FCSTD DOCUMENT  (FreeCAD 0.18.4R)
Label: CL260-Carrier-E3D-Titan
License: All rights reserved
LicenseURL: http://en.wikipedia.org/wiki/All_rights_reserved
objects: Sketcher::SketchObject×66, PartDesign::Pad×38, PartDesign::Plane×32, Part::Feature×21, PartDesign::Pocket×19, Part::Mirroring×19, PartDesign::Body×12, PartDesign::ShapeBinder×7, PartDesign::FeatureBase×6, PartDesign::Line×5, App::DocumentObjectGroup×4, Mesh::Feature×2, PartDesign::Mirrored×2, PartDesign::PolarPattern×2, App::Part×1, PartDesign::Fillet×1, PartDesign::Revolution×1, PartDesign::Groove×1
note: 291 computed .brp shape members not serialized (recipe doc carries the construction recipe); baked Part::Feature solids carry a one-line shape summary decoded from their .brp

FEATURE [Sketcher::SketchObject] Sketch  label="BaseSketch_XAxis"
  MapMode = 5
  Placement = pos=(0,0,0) rot=(0.57735,0.57735,0.57735;2.0944rad)
  Support = -> [YZ_Plane]
  expr: Constraints[1] = BaseDimensions.Constraints.Radius_Aussen_Achsenlagerkörper
  expr: Constraints[0] = Sketch003.Constraints.Radius_Achse
  sketch-geometry (1):
    g0: Circle CenterX=-11 CenterY=0 CenterZ=0 NormalX=0 NormalY=0 NormalZ=1 AngleXU=0 Radius=4
  constraints (3):
    c: Radius(g0) = 4
    c: DistanceX(g0,g-1) = 11
    c: PointOnObject(g0,g-1)
FEATURE [PartDesign::Line] DatumLine  label="X-Axis-DatumLine"
  AttacherType = Attacher::AttachEngineLine
  MapMode = 19
  Placement = pos=(-1.2408e-12,-11,1.242e-12) rot=(0.57735,0.57735,0.57735;2.0944rad)
  Support = -> [Sketch]
FEATURE [Sketcher::SketchObject] Sketch001  label="BaseSketch_YAxis"
  ExternalGeometry = -> [DatumLine]
  MapMode = 5
  Placement = pos=(0,0,0) rot=(1,0,0;1.5708rad)
  Support = -> [XZ_Plane]
  expr: Constraints[2] = BaseDimensions.Constraints.Abstand_HorizontalerAchsenabstand
  expr: Constraints[1] = BaseDimensions.Constraints.Abstand_VerticalerAchsenabstand
  expr: Constraints[0] = Sketch003.Constraints.Radius_Achse
  sketch-geometry (1):
    g0: Circle CenterX=-1 CenterY=-18 CenterZ=0 NormalX=0 NormalY=0 NormalZ=1 AngleXU=0 Radius=4
  constraints (3):
    c: Radius(g0) = 4
    c: DistanceY(g0,g-1) = 18
    c: DistanceX(g0,g-1) = 1
FEATURE [PartDesign::Line] DatumLine001  label="Y-Axis-DatumLine"
  AttacherType = Attacher::AttachEngineLine
  MapMode = 19
  Placement = pos=(-1,1.8545e-12,-18) rot=(1,0,0;1.5708rad)
  Support = -> [Sketch001]
FEATURE [Sketcher::SketchObject] Sketch003  label="BaseDimensions"
  MapMode = 5
  Support = -> [XY_Plane]
  sketch-geometry (15):
    g0: LineSegment [constr] StartX=-56.7363 StartY=18.8275 StartZ=0 EndX=-55.7363 EndY=18.8275 EndZ=0
    g1: LineSegment [constr] StartX=-54.0832 StartY=19.0838 StartZ=0 EndX=-54.0832 EndY=1.08377 EndZ=0
    g2: Circle [constr] CenterX=-26.2433 CenterY=17.2317 CenterZ=0 NormalX=0 NormalY=0 NormalZ=1 AngleXU=0 Radius=7.65
    g3: Circle [constr] CenterX=-26.2433 CenterY=17.2317 CenterZ=0 NormalX=0 NormalY=0 NormalZ=1 AngleXU=0 Radius=11
    g4: Circle [constr] CenterX=-26.2433 CenterY=17.2317 CenterZ=0 NormalX=0 NormalY=0 NormalZ=1 AngleXU=0 Radius=4
    g5: LineSegment [constr] StartX=-26.6458 StartY=-5.59924 StartZ=0 EndX=-2.64579 EndY=-5.59924 EndZ=0
    g6: LineSegment [constr] StartX=-23.9154 StartY=-12.201 StartZ=0 EndX=-21.4154 EndY=-12.201 EndZ=0
    g7: LineSegment [constr] StartX=-24.8331 StartY=-20.4604 StartZ=0 EndX=-21.8331 EndY=-20.4604 EndZ=0
    g8: Circle [constr] CenterX=-71.3028 CenterY=-13.3844 CenterZ=0 NormalX=0 NormalY=0 NormalZ=1 AngleXU=0 Radius=1.85
    g9: LineSegment [constr] StartX=-63.2198 StartY=35.4421 StartZ=0 EndX=-27.8698 EndY=35.4421 EndZ=0
    g10: LineSegment [constr] StartX=-62.0053 StartY=53.3997 StartZ=0 EndX=-12.0053 EndY=53.3997 EndZ=0
    g11: LineSegment [constr] StartX=-62.1011 StartY=68.6634 StartZ=0 EndX=-47.1011 EndY=68.6634 EndZ=0
    g12: LineSegment [constr] StartX=-62.8302 StartY=84.8991 StartZ=0 EndX=-39.3302 EndY=84.8991 EndZ=0
    g13: LineSegment [constr] StartX=-60.5898 StartY=95.611 StartZ=0 EndX=-50.5898 EndY=95.611 EndZ=0
    g14: Circle [constr] CenterX=-26.2433 CenterY=17.2317 CenterZ=0 NormalX=0 NormalY=0 NormalZ=1 AngleXU=0 Radius=7.7
  constraints (21):
    c: Radius(g2) = 7.65  'Radius_Igus_Innen_Y'
    c: Radius(g3) = 11  'Radius_Aussen_Achsenlagerkörper'
    c: Radius(g4) = 4  'Radius_Achse'
    c: DistanceY(g1,g1) = 18  'Abstand_VerticalerAchsenabstand'
    c: DistanceX(g0,g0) = 1  'Abstand_HorizontalerAchsenabstand'
    c: DistanceX(g5,g5) = 24  'Length_IgusBearing'
    c: DistanceX(g6,g6) = 2.5  'Thickness_Mountingbracket'
    c: DistanceX(g7,g7) = 3  'TitanMountPlate_ExtraThickness'
    c: Radius(g8) = 1.85  'Radius_Einpresshülse'
    c: Horizontal(g9)
    c: DistanceX(g9,g9) = 35.35  'Abstand_Löcher_TitanHalter'
    c: Horizontal(g10)
    c: DistanceX(g10,g10) = 50  'Länge_NemaHalter'
    c: Horizontal(g11)
    c: DistanceX(g11,g11) = 15  'Höhe_Lüfterwand'
    c: Horizontal(g12)
    c: DistanceX(g12,g12) = 23.5  'Länge_FanTisch'
    c: Horizontal(g13)
    c: DistanceX(g13,g13) = 10  'Länge_Überhang_FanTisch'
    c: Coincident(g14,g2)
    c: Radius(g14) = 7.7  'Radius_Igus_Innen_X'
FEATURE [Sketcher::SketchObject] Sketch004  label="YAchseBearingHolder"
  ExternalGeometry = -> [DatumLine001]
  MapMode = 5
  Placement = pos=(0,0,0) rot=(1,0,0;1.5708rad)
  Support = -> [XZ_Plane]
  expr: Constraints[1] = BaseDimensions.Constraints.Radius_Aussen_Achsenlagerkörper
  sketch-geometry (1):
    g0: Circle CenterX=-1 CenterY=-18 CenterZ=0 NormalX=0 NormalY=0 NormalZ=1 AngleXU=0 Radius=11
  constraints (2):
    c: Coincident(g0,g-3)
    c: Radius(g0) = 11
FEATURE [PartDesign::Pad] Pad  label="Pad_YAchseBearingHolder"
  Length = 48
  Length2 = 100
  Placement = pos=(0,0,0) rot=(1,0,0;1.5708rad)
  Profile = -> Sketch004
  Type = 0
  expr: Length = 2 * BaseDimensions.Constraints.Length_IgusBearing
FEATURE [Sketcher::SketchObject] Sketch005  label="XAchseBearingHolder"
  ExternalGeometry = -> [DatumLine]
  MapMode = 5
  Placement = pos=(0,0,0) rot=(0.57735,0.57735,0.57735;2.0944rad)
  Support = -> [YZ_Plane]
  expr: Constraints[1] = BaseDimensions.Constraints.Radius_Aussen_Achsenlagerkörper
  sketch-geometry (1):
    g0: Circle CenterX=-11 CenterY=0 CenterZ=0 NormalX=0 NormalY=0 NormalZ=1 AngleXU=0 Radius=11
  constraints (2):
    c: Coincident(g0,g-3)
    c: Radius(g0) = 11
FEATURE [PartDesign::Pad] Pad001  label="Pad_XAchseBearingHolder"
  BaseFeature = -> Pad
  Length = 48
  Length2 = 100
  Placement = pos=(0,0,0) rot=(1,0,0;1.5708rad)
  Profile = -> Sketch005
  Reversed = true
  Type = 0
  expr: Length = 2 * BaseDimensions.Constraints.Length_IgusBearing
FEATURE [PartDesign::Plane] DatumPlane  label="XAchseBearingHolderSeite1"
  Length = 30.3498
  MapMode = 11
  Placement = pos=(-1.2408e-12,-11,1.242e-12) rot=(0.707107,0,-0.707107;3.14159rad)
  ResizeMode = 0
  Support = -> [Sketch005]
  Width = 48.3498
FEATURE [Sketcher::SketchObject] Sketch006  label="Bracket"
  ExternalGeometry = -> [DatumLine]
  MapMode = 5
  Placement = pos=(-1.2408e-12,-11,1.242e-12) rot=(0.707107,0,-0.707107;3.14159rad)
  Support = -> [DatumPlane]
  expr: Constraints[9] = 2 * BaseDimensions.Constraints.Length_IgusBearing
  expr: Constraints[8] = BaseDimensions.Constraints.Radius_Aussen_Achsenlagerkörper
  expr: Constraints[4] = 2 * BaseDimensions.Constraints.Length_IgusBearing - BaseDimensions.Constraints.Radius_Aussen_Achsenlagerkörper
  sketch-geometry (4):
    g0: LineSegment StartX=10.8613 StartY=37 StartZ=0 EndX=-10.918 EndY=37 EndZ=0
    g1: LineSegment StartX=-10.918 StartY=37 StartZ=0 EndX=-10.918 EndY=-11 EndZ=0
    g2: LineSegment StartX=10.8613 StartY=-11 StartZ=0 EndX=10.8613 EndY=37 EndZ=0
    g3: LineSegment StartX=-10.918 StartY=-11 StartZ=0 EndX=10.8613 EndY=-11 EndZ=0
  constraints (10):
    c: Coincident(g0,g1)
    c: Coincident(g2,g0)
    c: Horizontal(g0)
    c: Vertical(g1)
    c: Vertical(g2) = 37
    c: Coincident(g3,g1)
    c: Coincident(g3,g2)
    c: Horizontal(g3)
    c: DistanceY(g2,g-1) = 11
    c: DistanceY(g2,g2) = 48
FEATURE [PartDesign::Pad] Pad002  label="Pad_Bracket"
  BaseFeature = -> Pad001
  Length = 2.5
  Length2 = 100
  Placement = pos=(0,0,0) rot=(1,0,0;1.5708rad)
  Profile = -> Sketch006
  Type = 0
  expr: Length = Sketch003.Constraints.Thickness_Mountingbracket
FEATURE [Sketcher::SketchObject] Sketch007
  ExternalGeometry = -> [DatumLine,DatumLine001]
  MapMode = 5
  Placement = pos=(-1.2408e-12,-11,1.242e-12) rot=(0.707107,0,-0.707107;3.14159rad)
  Support = -> [DatumPlane]
  expr: Constraints[10] = 1 * BaseDimensions.Constraints.Radius_Aussen_Achsenlagerkörper
  expr: Constraints[9] = BaseDimensions.Constraints.Radius_Aussen_Achsenlagerkörper
  expr: Constraints[8] = BaseDimensions.Constraints.Radius_Aussen_Achsenlagerkörper
  sketch-geometry (4):
    g0: LineSegment StartX=-11 StartY=11 StartZ=0 EndX=18 EndY=11 EndZ=0
    g1: LineSegment StartX=18 StartY=11 StartZ=0 EndX=18 EndY=-11 EndZ=0
    g2: LineSegment StartX=18 StartY=-11 StartZ=0 EndX=-11 EndY=-11 EndZ=0
    g3: LineSegment StartX=-11 StartY=-11 StartZ=0 EndX=-11 EndY=11 EndZ=0
  constraints (12):
    c: Coincident(g0,g1)
    c: Coincident(g1,g2)
    c: Coincident(g2,g3)
    c: Coincident(g3,g0)
    c: Horizontal(g0)
    c: Horizontal(g2)
    c: Vertical(g1)
    c: Vertical(g3)
    c: DistanceX(g0,g-3) = 11
    c: DistanceY(g-3,g0) = 11
    c: DistanceY(g2,g-3) = 11
    c: PointOnObject(g1,g-4)
FEATURE [PartDesign::Pad] Pad003  label="YAxisSupport"
  BaseFeature = -> Pad002
  Length = 12
  Length2 = 100
  Placement = pos=(0,0,0) rot=(1,0,0;1.5708rad)
  Profile = -> Sketch007
  Type = 0
  expr: Length = BaseDimensions.Constraints.Abstand_HorizontalerAchsenabstand + BaseDimensions.Constraints.Radius_Aussen_Achsenlagerkörper
FEATURE [Sketcher::SketchObject] Sketch008
  ExternalGeometry = -> [DatumLine]
  MapMode = 5
  Placement = pos=(0,0,0) rot=(0.57735,0.57735,0.57735;2.0944rad)
  Support = -> [YZ_Plane]
  expr: Constraints[11] = BaseDimensions.Constraints.Radius_Aussen_Achsenlagerkörper + BaseDimensions.Constraints.TitanMountPlate_ExtraThickness
  expr: Constraints[10] = BaseDimensions.Constraints.Radius_Aussen_Achsenlagerkörper
  expr: Constraints[9] = BaseDimensions.Constraints.Radius_Aussen_Achsenlagerkörper
  sketch-geometry (4):
    g0: LineSegment StartX=-22 StartY=14 StartZ=0 EndX=0 EndY=14 EndZ=0
    g1: LineSegment StartX=0 StartY=14 StartZ=0 EndX=0 EndY=0 EndZ=0
    g2: LineSegment StartX=0 StartY=0 StartZ=0 EndX=-22 EndY=0 EndZ=0
    g3: LineSegment StartX=-22 StartY=0 StartZ=0 EndX=-22 EndY=14 EndZ=0
  constraints (12):
    c: Coincident(g0,g1)
    c: Coincident(g1,g2)
    c: Coincident(g2,g3)
    c: Coincident(g3,g0)
    c: Horizontal(g0)
    c: Horizontal(g2)
    c: Vertical(g1)
    c: Vertical(g3)
    c: PointOnObject(g-3,g2)
    c: DistanceX(g2,g-3) = 11
    c: DistanceX(g-3,g1) = 11
    c: DistanceY(g1,g1) = 14
FEATURE [PartDesign::Pad] Pad004  label="TitanTable"
  BaseFeature = -> Pad003
  Length = 48
  Length2 = 100
  Placement = pos=(0,0,0) rot=(1,0,0;1.5708rad)
  Profile = -> Sketch008
  Reversed = true
  Type = 0
  expr: Length = 2 * BaseDimensions.Constraints.Length_IgusBearing
FEATURE [PartDesign::Plane] DatumPlane001  label="X-Support-End-DatumPlane"
  AttachmentOffset = pos=(0,0,48) rot=(0,0,1;0rad)
  Length = 30.3498
  MapMode = 9
  Placement = pos=(-48,-7,-4.6266e-12) rot=(0.707107,0,-0.707107;3.14159rad)
  ResizeMode = 0
  Support = -> [Sketch]
  Width = 48.3498
  expr: AttachmentOffset.Base.z = 2 * BaseDimensions.Constraints.Length_IgusBearing
FEATURE [Sketcher::SketchObject] Sketch009
  ExternalGeometry = -> [DatumLine]
  MapMode = 5
  Placement = pos=(-48,-7,-4.6266e-12) rot=(0.707107,0,-0.707107;3.14159rad)
  Support = -> [DatumPlane001]
  expr: Constraints[1] = Sketch003.Constraints.Radius_Igus_Innen_X
  sketch-geometry (1):
    g0: Circle CenterX=0 CenterY=4 CenterZ=0 NormalX=0 NormalY=0 NormalZ=1 AngleXU=0 Radius=7.7
  constraints (2):
    c: Coincident(g0,g-3)
    c: Radius(g0) = 7.7
FEATURE [PartDesign::Pocket] Pocket  label="Pocket_X-Bearing"
  BaseFeature = -> Pad004
  Length = 5
  Length2 = 100
  Placement = pos=(0,0,0) rot=(1,0,0;1.5708rad)
  Profile = -> Sketch009
  Type = 1
FEATURE [Sketcher::SketchObject] Sketch010
  ExternalGeometry = -> [DatumLine001]
  MapMode = 5
  Placement = pos=(0,0,0) rot=(1,0,0;1.5708rad)
  Support = -> [XZ_Plane]
  expr: Constraints[1] = Sketch003.Constraints.Radius_Igus_Innen_Y
  sketch-geometry (1):
    g0: Circle CenterX=-1 CenterY=-18 CenterZ=0 NormalX=0 NormalY=0 NormalZ=1 AngleXU=0 Radius=7.65
  constraints (2):
    c: Coincident(g0,g-3)
    c: Radius(g0) = 7.65
FEATURE [PartDesign::Pocket] Pocket001  label="Pocket_Y-Bearing"
  BaseFeature = -> Pocket
  Length = 5
  Length2 = 100
  Placement = pos=(0,0,0) rot=(1,0,0;1.5708rad)
  Profile = -> Sketch010
  Reversed = true
  Type = 1
FEATURE [PartDesign::Plane] DatumPlane002  label="TitanMountTable_DatumPlane"
  AttachmentOffset = pos=(0,0,14) rot=(0,0,1;0rad)
  Length = 55.1545
  MapMode = 3
  Placement = pos=(-2.8207e-12,-11,14) rot=(0,0,-1;1.5708rad)
  ResizeMode = 0
  Support = -> [DatumLine]
  Width = 116.154
  expr: AttachmentOffset.Base.z = BaseDimensions.Constraints.Radius_Aussen_Achsenlagerkörper + BaseDimensions.Constraints.TitanMountPlate_ExtraThickness
FEATURE [Sketcher::SketchObject] Sketch011
  ExternalGeometry = -> [DatumLine,Pocket001,DatumPlane001]
  MapMode = 5
  Placement = pos=(-2.8207e-12,-11,14) rot=(0,0,-1;1.5708rad)
  Support = -> [DatumPlane002]
  expr: Constraints[3] = BaseDimensions.Constraints.Radius_Einpresshülse
  sketch-geometry (5):
    g0: Circle CenterX=-7.4 CenterY=-6.325 CenterZ=0 NormalX=0 NormalY=0 NormalZ=1 AngleXU=0 Radius=1.85
    g1: Circle CenterX=-7.4 CenterY=-41.675 CenterZ=0 NormalX=0 NormalY=0 NormalZ=1 AngleXU=0 Radius=1.85
    g2: LineSegment [constr] StartX=-7.4 StartY=-6.325 StartZ=0 EndX=-7.4 EndY=-41.675 EndZ=0
    g3: LineSegment [constr] StartX=-7.4 StartY=-48 StartZ=0 EndX=-7.4 EndY=-41.675 EndZ=0
    g4: LineSegment [constr] StartX=-7.4 StartY=-6.325 StartZ=0 EndX=-7.4 EndY=0 EndZ=0
  constraints (14):
    c: Coincident(g0,g2)
    c: Coincident(g2,g1)
    c: Parallel(g2,g-3)
    c: Radius(g1) = 1.85
    c: Equal(g1,g0)
    c: DistanceY(g2,g2) = 35.35
    c: DistanceX(g-4,g0) = 3.6
    c: PointOnObject(g3,g-5)
    c: Vertical(g3)
    c: Coincident(g3,g1)
    c: Coincident(g4,g0)
    c: Vertical(g4)
    c: Equal(g4,g3)
    c: PointOnObject(g4,g-1)
FEATURE [PartDesign::Pocket] Pocket002  label="Titan_MountingHoles"
  BaseFeature = -> Pocket001
  Length = 8.5
  Length2 = 100
  Placement = pos=(0,0,0) rot=(1,0,0;1.5708rad)
  Profile = -> Sketch011
  Type = 0
FEATURE [Sketcher::SketchObject] Sketch012
  ExternalGeometry = -> [DatumPlane002,DatumLine]
  MapMode = 5
  Placement = pos=(-1.2408e-12,-11,1.242e-12) rot=(0.707107,0,-0.707107;3.14159rad)
  Support = -> [DatumPlane]
  expr: Constraints[9] = 2 * BaseDimensions.Constraints.Radius_Aussen_Achsenlagerkörper
  sketch-geometry (4):
    g0: LineSegment StartX=-14 StartY=11 StartZ=0 EndX=-11 EndY=11 EndZ=0
    g1: LineSegment StartX=-11 StartY=11 StartZ=0 EndX=-11 EndY=-11 EndZ=0
    g2: LineSegment StartX=-11 StartY=-11 StartZ=0 EndX=-14 EndY=-11 EndZ=0
    g3: LineSegment StartX=-14 StartY=-11 StartZ=0 EndX=-14 EndY=11 EndZ=0
  constraints (11):
    c: Coincident(g0,g1)
    c: Coincident(g1,g2)
    c: Coincident(g2,g3)
    c: Coincident(g3,g0)
    c: Horizontal(g0)
    c: Horizontal(g2)
    c: Vertical(g3)
    c: PointOnObject(g0,g-3)
    c: Symmetric(g1,g0,g-1)
    c: DistanceY(g1,g1) = 22
    c: DistanceX(g2,g2) = 3
FEATURE [Sketcher::SketchObject] Sketch013
  ExternalGeometry = -> [DatumPlane002,DatumLine]
  MapMode = 5
  Placement = pos=(-48,-7,-4.6266e-12) rot=(0.707107,0,-0.707107;3.14159rad)
  Support = -> [DatumPlane001]
  expr: Constraints[11] = BaseDimensions.Constraints.TitanMountPlate_ExtraThickness
  expr: Constraints[10] = 2 * BaseDimensions.Constraints.Radius_Aussen_Achsenlagerkörper
  expr: Constraints[9] = BaseDimensions.Constraints.Radius_Aussen_Achsenlagerkörper
  sketch-geometry (4):
    g0: LineSegment StartX=-14 StartY=15 StartZ=0 EndX=-11 EndY=15 EndZ=0
    g1: LineSegment StartX=-11 StartY=15 StartZ=0 EndX=-11 EndY=-7 EndZ=0
    g2: LineSegment StartX=-11 StartY=-7 StartZ=0 EndX=-14 EndY=-7 EndZ=0
    g3: LineSegment StartX=-14 StartY=-7 StartZ=0 EndX=-14 EndY=15 EndZ=0
  constraints (12):
    c: Coincident(g0,g1)
    c: Coincident(g1,g2)
    c: Coincident(g2,g3)
    c: Coincident(g3,g0)
    c: Horizontal(g0)
    c: Horizontal(g2)
    c: Vertical(g1)
    c: Vertical(g3)
    c: PointOnObject(g0,g-3)
    c: DistanceY(g-4,g0) = 11
    c: DistanceY(g1,g1) = 22
    c: DistanceX(g0,g0) = 3
FEATURE [Sketcher::SketchObject] Sketch014
  ExternalGeometry = -> [DatumLine001]
  MapMode = 5
  Placement = pos=(0,0,0) rot=(1,0,0;1.5708rad)
  Support = -> [XZ_Plane]
  expr: Constraints[10] = BaseDimensions.Constraints.Radius_Igus_Innen_Y + 2mm
  expr: Constraints[8] = BaseDimensions.Constraints.Radius_Aussen_Achsenlagerkörper
  sketch-geometry (4):
    g0: LineSegment StartX=11 StartY=-10.3416 StartZ=0 EndX=11 EndY=0 EndZ=0
    g1: LineSegment StartX=11 StartY=0 StartZ=0 EndX=0 EndY=0 EndZ=0
    g2: LineSegment StartX=0 StartY=0 StartZ=0 EndX=0 EndY=-8.40195 EndZ=0
    g3: LineSegment StartX=11 StartY=-10.3416 StartZ=0 EndX=0 EndY=-8.40195 EndZ=0
  constraints (11):
    c: Coincident(g0,g1)
    c: Coincident(g1,g2)
    c: Horizontal(g1)
    c: Vertical(g0)
    c: Vertical(g2)
    c: Coincident(g3,g0)
    c: Coincident(g3,g2)
    c: Coincident(g-1,g1)
    c: DistanceX(g1,g1) = 11
    c: Angle(g3,g2) = 1.74533
    c: Distance(g-3,g2) = 9.65
FEATURE [PartDesign::Pocket] Pocket003
  BaseFeature = -> Pocket002
  Length = 24
  Length2 = 100
  Placement = pos=(0,0,0) rot=(1,0,0;1.5708rad)
  Profile = -> Sketch014
  Reversed = true
  Type = 0
  expr: Length = 2mm + 2 * BaseDimensions.Constraints.Radius_Aussen_Achsenlagerkörper
FEATURE [Sketcher::SketchObject] Sketch016
  ExternalGeometry = -> [DatumLine001]
  MapMode = 5
  Placement = pos=(-1.2408e-12,-11,1.242e-12) rot=(0.707107,0,-0.707107;3.14159rad)
  Support = -> [DatumPlane]
  expr: Constraints[28] = BaseDimensions.Constraints.Radius_Aussen_Achsenlagerkörper
  expr: Constraints[10] = BaseDimensions.Constraints.Radius_Einpresshülse
  sketch-geometry (10):
    g0: LineSegment StartX=-3 StartY=34 StartZ=0 EndX=7 EndY=34 EndZ=0
    g1: LineSegment StartX=7 StartY=34 StartZ=0 EndX=7 EndY=14 EndZ=0
    g2: LineSegment StartX=7 StartY=14 StartZ=0 EndX=-3 EndY=14 EndZ=0
    g3: LineSegment StartX=-3 StartY=14 StartZ=0 EndX=-3 EndY=34 EndZ=0
    g4: Circle CenterX=-7 CenterY=33 CenterZ=0 NormalX=0 NormalY=0 NormalZ=1 AngleXU=0 Radius=1.85
    g5: Circle CenterX=-7 CenterY=27 CenterZ=0 NormalX=0 NormalY=0 NormalZ=1 AngleXU=0 Radius=1.85
    g6: Circle CenterX=-7 CenterY=21 CenterZ=0 NormalX=0 NormalY=0 NormalZ=1 AngleXU=0 Radius=1.85
    g7: Circle CenterX=-7 CenterY=15 CenterZ=0 NormalX=0 NormalY=0 NormalZ=1 AngleXU=0 Radius=1.85
    g8: LineSegment [constr] StartX=-7 StartY=34 StartZ=0 EndX=-7 EndY=14 EndZ=0
    g9: LineSegment [constr] StartX=7 StartY=34 StartZ=0 EndX=18 EndY=34 EndZ=0
  constraints (31):
    c: Coincident(g0,g1)
    c: Coincident(g1,g2)
    c: Coincident(g2,g3)
    c: Coincident(g3,g0)
    c: Horizontal(g0)
    c: Horizontal(g2)
    c: Vertical(g1)
    c: Vertical(g3)
    c: DistanceX(g0,g0) = 10
    c: DistanceY(g3,g3) = 20
    c: Radius(g7) = 1.85
    c: Equal(g7,g6)
    c: Equal(g7,g5)
    c: Equal(g7,g4)
    c: DistanceY(g5,g4) = 6
    c: DistanceY(g6,g5) = 6
    c: DistanceY(g7,g6) = 6
    c: Vertical(g8)
    c: PointOnObject(g7,g8)
    c: PointOnObject(g6,g8)
    c: PointOnObject(g5,g8)
    c: PointOnObject(g4,g8)
    c: DistanceY(g-1,g1) = 14
    c: DistanceY(g2,g7) = 1
    c: DistanceX(g7,g2) = 4
    c: Coincident(g9,g0)
    c: PointOnObject(g9,g-3)
    c: Horizontal(g9)
    c: DistanceX(g9,g9) = 11
    c: PointOnObject(g8,g0)
    c: PointOnObject(g8,g2)
FEATURE [PartDesign::Pocket] Pocket005  label="Fanduct-Holes"
  BaseFeature = -> Pocket003
  Length = 5
  Length2 = 100
  Placement = pos=(0,0,0) rot=(1,0,0;1.5708rad)
  Profile = -> Sketch016
  Reversed = true
  Type = 0
FEATURE [PartDesign::Plane] DatumPlane003  label="InnensSeite_X-AchsenBearingHalter"
  AttachmentOffset = pos=(0,0,22) rot=(0,0,1;0rad)
  Length = 112.944
  MapMode = 2
  Placement = pos=(0,-22,-2.2679e-12) rot=(1,0,0;1.5708rad)
  ResizeMode = 0
  Support = -> [Sketch001]
  Width = 33.9438
  expr: AttachmentOffset.Base.z = 2 * BaseDimensions.Constraints.Radius_Aussen_Achsenlagerkörper
FEATURE [Sketcher::SketchObject] Sketch017
  ExternalGeometry = -> [DatumLine,DatumPlane001]
  MapMode = 5
  Placement = pos=(0,-22,-2.2679e-12) rot=(1,0,0;1.5708rad)
  Support = -> [DatumPlane003]
  expr: Constraints[14] = 0.25mm + BaseDimensions.Constraints.Radius_Aussen_Achsenlagerkörper - BaseDimensions.Constraints.Radius_Einpresshülse
  expr: Constraints[0] = BaseDimensions.Constraints.Radius_Einpresshülse
  sketch-geometry (7):
    g0: Circle CenterX=-45.5 CenterY=9.4 CenterZ=0 NormalX=0 NormalY=0 NormalZ=1 AngleXU=0 Radius=1.85
    g1: Circle CenterX=-35.5 CenterY=9.4 CenterZ=0 NormalX=0 NormalY=0 NormalZ=1 AngleXU=0 Radius=1.85
    g2: Circle CenterX=-10.5 CenterY=9.4 CenterZ=0 NormalX=0 NormalY=0 NormalZ=1 AngleXU=0 Radius=1.85
    g3: Circle CenterX=-20.5 CenterY=9.4 CenterZ=0 NormalX=0 NormalY=0 NormalZ=1 AngleXU=0 Radius=1.85
    g4: LineSegment [constr] StartX=-45.5 StartY=9.4 StartZ=0 EndX=-45.5 EndY=-3.0003e-12 EndZ=0
    g5: LineSegment [constr] StartX=-45.5 StartY=9.4 StartZ=0 EndX=-10.5 EndY=9.4 EndZ=0
    g6: LineSegment [constr] StartX=-48 StartY=9.4 StartZ=0 EndX=-45.5 EndY=9.4 EndZ=0
  constraints (20):
    c: Radius(g2) = 1.85
    c: Equal(g2,g3)
    c: Equal(g2,g1)
    c: Equal(g2,g0)
    c: Coincident(g4,g0)
    c: PointOnObject(g4,g-3)
    c: Vertical(g4)
    c: Coincident(g5,g0)
    c: Coincident(g5,g2)
    c: Horizontal(g5)
    c: PointOnObject(g1,g5)
    c: PointOnObject(g3,g5)
    c: DistanceX(g0,g1) = 10
    c: DistanceX(g3,g2) = 10
    c: DistanceY(g4,g4) = 9.4
    c: DistanceX(g1,g3) = 15
    c: Horizontal(g6)
    c: PointOnObject(g6,g-4)
    c: Coincident(g6,g0)
    c: DistanceX(g6,g6) = 2.5
FEATURE [PartDesign::Pocket] Pocket006  label="MoreHoles"
  BaseFeature = -> Pocket005
  Length = 8
  Length2 = 100
  Placement = pos=(0,0,0) rot=(1,0,0;1.5708rad)
  Profile = -> Sketch017
  Type = 0
FEATURE [PartDesign::Line] DatumLine005
  AttacherType = Attacher::AttachEngineLine
  MapMode = 19
  Placement = pos=(-6.325,-3.6,14) rot=(0,0,1;4.71239rad)
  Support = -> [Sketch011]
FEATURE [PartDesign::Line] DatumLine006
  AttacherType = Attacher::AttachEngineLine
  MapMode = 19
  Placement = pos=(-41.675,-3.6,14) rot=(0,0,1;4.71239rad)
  Support = -> [Sketch011]
FEATURE [PartDesign::Plane] DatumPlane004  label="TitanHolderMiddlePlane"
  AttachmentOffset = pos=(0,0,-17.675) rot=(0,0,1;0rad)
  Length = 48.3498
  MapMode = 14
  Placement = pos=(-24,-3.6,14) rot=(-0.57735,0.57735,0.57735;4.18879rad)
  ResizeMode = 0
  Support = -> [DatumLine006,DatumLine005]
  Width = 30.3498
  expr: AttachmentOffset.Base.z = -BaseDimensions.Constraints.Abstand_Löcher_TitanHalter / 2
FEATURE [Sketcher::SketchObject] Sketch024
  ExternalGeometry = -> [DatumPlane001]
  MapMode = 5
  Placement = pos=(0,-22,-2.2679e-12) rot=(1,0,0;1.5708rad)
  Support = -> [DatumPlane003]
  sketch-geometry (4):
    g0: LineSegment StartX=-40 StartY=-7.75 StartZ=0 EndX=-12 EndY=-7.75 EndZ=0
    g1: LineSegment StartX=-12 StartY=-7.75 StartZ=0 EndX=-12 EndY=-15.056 EndZ=0
    g2: LineSegment StartX=-12 StartY=-15.056 StartZ=0 EndX=-40 EndY=-15.056 EndZ=0
    g3: LineSegment StartX=-40 StartY=-15.056 StartZ=0 EndX=-40 EndY=-7.75 EndZ=0
  constraints (11):
    c: Coincident(g0,g1)
    c: Coincident(g1,g2)
    c: Coincident(g2,g3)
    c: Coincident(g3,g0)
    c: Horizontal(g0)
    c: Horizontal(g2)
    c: Vertical(g1)
    c: Vertical(g3)
    c: DistanceX(g0,g0) = 28
    c: DistanceY(g0,g-1) = 7.75
    c: Distance(g0,g-3) = 8
FEATURE [PartDesign::Plane] DatumPlane005
  Length = 43.4822
  MapMode = 11
  Placement = pos=(-1,1.8545e-12,-18) rot=(0.57735,-0.57735,0.57735;2.0944rad)
  ResizeMode = 0
  Support = -> [Sketch004]
  Width = 114.482
FEATURE [Mesh::Feature] titan_aero_holder_v5
  Placement = pos=(-55,-32.5,4.1) rot=(-1,0,0;3.14159rad)
FEATURE [Part::Feature] _0mm_Fan001  label="50mm-Fan"
  Placement = pos=(-52,-22,24) rot=(0,-1,0;1.5708rad)
  shape: bbox 15 x 51.49 x 51.5 mm, 1034 faces, 0 solids (baked)
FEATURE [Sketcher::SketchObject] Sketch032
  MapMode = 5
  Placement = pos=(-1.2408e-12,-11,1.242e-12) rot=(0.707107,0,-0.707107;3.14159rad)
  Support = -> [DatumPlane]
  expr: Constraints[0] = BaseDimensions.Constraints.Radius_Aussen_Achsenlagerkörper - 1mm
  sketch-geometry (8):
    g0: Circle CenterX=0 CenterY=0 CenterZ=0 NormalX=0 NormalY=0 NormalZ=1 AngleXU=0 Radius=10
    g1: LineSegment StartX=0 StartY=6 StartZ=0 EndX=-5.19615 EndY=3 EndZ=0
    g2: LineSegment StartX=-5.19615 StartY=3 StartZ=0 EndX=-5.19615 EndY=-3 EndZ=0
    g3: LineSegment StartX=-5.19615 StartY=-3 StartZ=0 EndX=0 EndY=-6 EndZ=0
    g4: LineSegment StartX=0 StartY=-6 StartZ=0 EndX=5.19615 EndY=-3 EndZ=0
    g5: LineSegment StartX=5.19615 StartY=-3 StartZ=0 EndX=5.19615 EndY=3 EndZ=0
    g6: LineSegment StartX=5.19615 StartY=3 StartZ=0 EndX=0 EndY=6 EndZ=0
    g7: Circle [constr] CenterX=0 CenterY=0 CenterZ=0 NormalX=0 NormalY=0 NormalZ=1 AngleXU=0 Radius=6
  constraints (18):
    c: Radius(g0) = 10
    c: Coincident(g1,g2)
    c: Coincident(g2,g3)
    c: Coincident(g3,g4)
    c: Coincident(g4,g5)
    c: Coincident(g5,g6)
    c: Coincident(g6,g1)
    c: Equal(g1, g2-g6) x5
    c: PointOnObject(g1,g7)
    c: PointOnObject(g2,g7)
    c: PointOnObject(g3,g7)
    c: PointOnObject(g4,g7)
    c: PointOnObject(g5,g7)
    c: PointOnObject(g6,g7)
    c: Coincident(g7,g-1)
    c: Radius(g7) = 6
    c: Vertical(g5)
    c: Coincident(g0,g-1)
FEATURE [PartDesign::Pad] Pad014  label="Hexnut-Anschlag-BearingX"
  BaseFeature = -> Pocket006
  Length = 1.5
  Length2 = 100
  Placement = pos=(0,0,0) rot=(1,0,0;1.5708rad)
  Profile = -> Sketch032
  Type = 0
FEATURE [Sketcher::SketchObject] Sketch033
  ExternalGeometry = -> [DatumLine001]
  MapMode = 5
  Placement = pos=(0,0,0) rot=(1,0,0;1.5708rad)
  Support = -> [XZ_Plane]
  expr: Constraints[1] = BaseDimensions.Constraints.Radius_Aussen_Achsenlagerkörper - 2mm
  sketch-geometry (8):
    g0: Circle CenterX=-1 CenterY=-18 CenterZ=0 NormalX=0 NormalY=0 NormalZ=1 AngleXU=0 Radius=9
    g1: LineSegment StartX=-4 StartY=-23.1962 StartZ=0 EndX=2 EndY=-23.1962 EndZ=0
    g2: LineSegment StartX=2 StartY=-23.1962 StartZ=0 EndX=5 EndY=-18 EndZ=0
    g3: LineSegment StartX=5 StartY=-18 StartZ=0 EndX=2 EndY=-12.8038 EndZ=0
    g4: LineSegment StartX=2 StartY=-12.8038 StartZ=0 EndX=-4 EndY=-12.8038 EndZ=0
    g5: LineSegment StartX=-4 StartY=-12.8038 StartZ=0 EndX=-7 EndY=-18 EndZ=0
    g6: LineSegment StartX=-7 StartY=-18 StartZ=0 EndX=-4 EndY=-23.1962 EndZ=0
    g7: Circle [constr] CenterX=-1 CenterY=-18 CenterZ=0 NormalX=0 NormalY=0 NormalZ=1 AngleXU=0 Radius=6
  constraints (18):
    c: Coincident(g0,g-3)
    c: Radius(g0) = 9
    c: Coincident(g1,g2)
    c: Coincident(g2,g3)
    c: Coincident(g3,g4)
    c: Coincident(g4,g5)
    c: Coincident(g5,g6)
    c: Coincident(g6,g1)
    c: Equal(g1, g2-g6) x5
    c: PointOnObject(g1,g7)
    c: PointOnObject(g2,g7)
    c: PointOnObject(g3,g7)
    c: PointOnObject(g4,g7)
    c: PointOnObject(g5,g7)
    c: PointOnObject(g6,g7)
    c: Coincident(g7,g0)
    c: Radius(g7) = 6
    c: Horizontal(g4)
FEATURE [PartDesign::Pad] Pad015  label="Hexnut-Anschlag-BearingY"
  BaseFeature = -> Pad014
  Length = 1.5
  Length2 = 100
  Placement = pos=(0,0,0) rot=(1,0,0;1.5708rad)
  Profile = -> Sketch033
  Type = 0
FEATURE [PartDesign::Pocket] Pocket007003  label="Heatsink_EnhanceAirFlow"
  BaseFeature = -> Pad015
  Length = 5
  Length2 = 100
  Placement = pos=(0,0,0) rot=(1,0,0;1.5708rad)
  Profile = -> Sketch024
  Type = 1
FEATURE [Part::Feature] Part__Feature020  label="ISO 4762 - M3 x 25ISO"
  Placement = pos=(28.5171,-8.05,-25) rot=(0,-1,0;1.5708rad)
  shape: bbox 5.953 x 5.953 x 28 mm, 15 faces (baked)
FEATURE [Part::Feature] Part__Feature008  label="M_BEARING_MR95ZZ"
  Placement = pos=(22.2171,-38.5563,-4) rot=(0.707107,0.000752,0.707107;3.1431rad)
  shape: bbox 9.742 x 9.742 x 3 mm, 55 faces, 13 solids (baked)
FEATURE [Part::Feature] Part__Feature001  label="Spur Gear21"
  Placement = pos=(0,22,0) rot=(0,0,1;3.09399rad)
  shape: bbox 34 x 33.98 x 4 mm, 267 faces (baked)
FEATURE [Part::Feature] Part__Feature009  label="M_BEARING_SMR74ZZ"
  Placement = pos=(22.2171,-38.5563,-20.75) rot=(0,1,0;1.5708rad)
  shape: bbox 9.742 x 9.742 x 3 mm, 55 faces, 13 solids (baked)
FEATURE [Part::Feature] Part__Feature014  label="EX_PIGNION"
  Placement = pos=(6.66075,-23,-0.4) rot=(-0.998967,-0.032133,0.032133;1.57183rad)
  shape: bbox 12.06 x 11.99 x 9 mm, 97 faces (baked)
FEATURE [Part::Feature] Part__Feature003  label="EX_EXTRUDER_LID (Edition 4)_Public"
  Placement = pos=(0.461723,-9.23586,-22) rot=(1,0,0;3.14159rad)
  shape: bbox 46.39 x 49.51 x 137 mm, 484 faces (baked)
FEATURE [Part::Mirroring] Part__Mirroring016  label="Spur Gear21 (Mirror #17)"
  Base = (0,0,0)
  Normal = (0,0,1)
  Placement = pos=(-23.13,-60.51,-5.8) rot=(0,0,-1;0.04119rad)
  Source = -> Part__Feature001
FEATURE [Part::Feature] Part__Feature017  label="ISO 4762 - M3 x 20ISO002"
  Placement = pos=(22.1608,-38.5,-25) rot=(0,-1,0;1.5708rad)
  shape: bbox 5.953 x 5.953 x 23 mm, 15 faces (baked)
FEATURE [Part::Feature] Part__Feature018  label="ANSI B18.2.4.2M - M4x0.7 - 7"
  Placement = pos=(-12.4308,-46,-13.5) rot=(1,0,0;2.0944rad)
  shape: bbox 3.8 x 8.083 x 8.083 mm, 23 faces (baked)
FEATURE [Part::Feature] Part__Feature012  label="Titan Idler Tension Screw v6"
  Placement = pos=(-20.0892,-46,-13.5) rot=(0,0,1;0rad)
  shape: bbox 18 x 15 x 15 mm, 12 faces (baked)
FEATURE [Part::Mirroring] Part__Mirroring005  label="Titan Idler Tension Screw v6 (Mirror #6)"
  Base = (0,0,0)
  Normal = (1,0,0)
  Source = -> Part__Feature012
FEATURE [Part::Feature] Part__Feature006  label="EX_EXTRUDER_BODY_2"
  Placement = pos=(6.66075,-23,-1) rot=(1,0,0;3.14159rad)
  shape: bbox 46.57 x 60.21 x 24.06 mm, 338 faces (baked)
FEATURE [Part::Mirroring] Part__Mirroring001  label="EX_EXTRUDER_BODY_2 (Mirror #2)"
  Base = (0,0,0)
  Normal = (1,0,0)
  Source = -> Part__Feature006
FEATURE [Part::Feature] Part__Feature016  label="ISO 4762 - M3 x 20ISO001"
  Placement = pos=(-8.83925,-38.5,-25) rot=(0,-1,0;1.5708rad)
  shape: bbox 5.953 x 5.953 x 23 mm, 15 faces (baked)
FEATURE [Part::Mirroring] Part__Mirroring009  label="ISO 4762 - M3 x 20ISO001 (Mirror #10)"
  Base = (0,0,0)
  Normal = (1,0,0)
  Source = -> Part__Feature016
FEATURE [Part::Mirroring] Part__Mirroring013  label="ISO 4762 - M3 x 25ISO (Mirror #14)"
  Base = (0,0,0)
  Normal = (1,0,0)
  Source = -> Part__Feature020
FEATURE [Part::Feature] Part__Feature013  label="PTFE_HOLDER (Edition 2)"
  Placement = pos=(11.7608,-16.3,-23.5) rot=(-1,-2e-06,-2e-06;1.5708rad)
  shape: bbox 11.22 x 59.29 x 16.4 mm, 201 faces (baked)
FEATURE [Part::Feature] Part__Feature015  label="ISO 4762 - M3 x 20ISO"
  Placement = pos=(-8.83925,-7.5,-25) rot=(0,-1,0;1.5708rad)
  shape: bbox 5.953 x 5.953 x 23 mm, 15 faces (baked)
FEATURE [Part::Mirroring] Part__Mirroring008  label="ISO 4762 - M3 x 20ISO (Mirror #9)"
  Base = (0,0,0)
  Normal = (1,0,0)
  Source = -> Part__Feature015
FEATURE [Part::Feature] Part__Feature019  label="ISO 4762 - M3 x 5ISO"
  Placement = pos=(22.1608,-7.5,-3) rot=(0.447214,-0.774597,0.447214;1.82348rad)
  shape: bbox 5.75 x 5.75 x 8 mm, 15 faces (baked)
FEATURE [Part::Feature] Part__Feature021  label="EX_IDLER_PIN_3mm"
  Placement = pos=(12.2108,-39,-17.5) rot=(0,0,1;0rad)
  shape: bbox 3 x 3 x 8 mm, 8 faces (baked)
FEATURE [Part::Mirroring] Part__Mirroring007  label="EX_PIGNION (Mirror #8)"
  Base = (0,0,0)
  Normal = (1,0,0)
  Source = -> Part__Feature014
FEATURE [Part::Feature] Part__Feature010  label="SOLID001"
  shape: bbox 12.72 x 6.873 x 6.873 mm, 3 faces (baked)
FEATURE [Part::Mirroring] Part__Mirroring017  label="SOLID001 (Mirror #18)"
  Base = (0,0,0)
  Normal = (0,0,1)
  Placement = pos=(8,-45,-13) rot=(0,0,1;0rad)
  Source = -> Part__Feature010
FEATURE [Part::Feature] Part__Feature007  label="IC_EXTRUDER_IDLER_2.1"
  Placement = pos=(6.66075,-23,-11.5) rot=(0.57735,0.57735,-0.57735;4.18879rad)
  shape: bbox 22.05 x 46.43 x 9.747 mm, 528 faces (baked)
FEATURE [Part::Mirroring] Part__Mirroring006  label="PTFE_HOLDER (Edition 2) (Mirror #7)"
  Base = (0,0,0)
  Normal = (1,0,0)
  Source = -> Part__Feature013
FEATURE [Part::Mirroring] Part__Mirroring011  label="ANSI B18.2.4.2M - M4x0.7 - 7 (Mirror #12)"
  Base = (0,0,0)
  Normal = (1,0,0)
  Source = -> Part__Feature018
FEATURE [Part::Mirroring] Part__Mirroring010  label="ISO 4762 - M3 x 20ISO002 (Mirror #11)"
  Base = (0,0,0)
  Normal = (1,0,0)
  Source = -> Part__Feature017
FEATURE [Part::Mirroring] Part__Mirroring014  label="EX_IDLER_PIN_3mm (Mirror #15)"
  Base = (0,0,0)
  Normal = (1,0,0)
  Source = -> Part__Feature021
FEATURE [Part::Mirroring] Part__Mirroring  label="EX_EXTRUDER_LID (Edition 4)_Public (Mirror #1)"
  Base = (0,0,0)
  Normal = (1,0,0)
  Source = -> Part__Feature003
FEATURE [Part::Feature] Part__Feature  label="M_HOBB_v2_EX_Blank"
  Placement = pos=(-22.724,-4.52781,-6.8) rot=(0,0,-1;0.0774rad)
  shape: bbox 10.3 x 10.3 x 20.5 mm, 17 faces (baked)
FEATURE [Part::Mirroring] Part__Mirroring015  label="M_HOBB_v2_EX_Blank (Mirror #16)"
  Base = (0,0,0)
  Normal = (0,0,1)
  Placement = pos=(0.5,-34,-11) rot=(0,0,1;0rad)
  Source = -> Part__Feature
FEATURE [Part::Mirroring] Part__Mirroring002  label="IC_EXTRUDER_IDLER_2.1 (Mirror #3)"
  Base = (0,0,0)
  Normal = (1,0,0)
  Source = -> Part__Feature007
FEATURE [Part::Mirroring] Part__Mirroring004  label="M_BEARING_SMR74ZZ (Mirror #5)"
  Base = (0,0,0)
  Normal = (1,0,0)
  Source = -> Part__Feature009
FEATURE [Part::Mirroring] Part__Mirroring003  label="M_BEARING_MR95ZZ (Mirror #4)"
  Base = (0,0,0)
  Normal = (1,0,0)
  Source = -> Part__Feature008
FEATURE [Part::Mirroring] Part__Mirroring012  label="ISO 4762 - M3 x 5ISO (Mirror #13)"
  Base = (0,0,0)
  Normal = (1,0,0)
  Source = -> Part__Feature019
FEATURE [Part::Feature] Part__Feature011  label="COMPOUND001"
  shape: bbox 1.02 x 2e-07 x 1.02 mm, 0 faces, 0 solids (baked)
FEATURE [Part::Mirroring] Part__Mirroring018  label="COMPOUND001 (Mirror #19)"
  Base = (0,0,0)
  Normal = (0,0,1)
  Source = -> Part__Feature011
FEATURE [App::Part] Part  label="E3D-Titan_mirrored"
  Group = -> [Part__Feature003,Part__Mirroring,Part__Feature006,Part__Mirroring001,Part__Feature007,Part__Mirroring002,Part__Feature008,Part__Mirroring003,Part__Feature009,Part__Mirroring004,Part__Feature012,Part__Mirroring005,Part__Feature013,Part__Mirroring006,Part__Feature014,Part__Mirroring007,Part__Feature015,Part__Mirroring008,Part__Feature016,Part__Mirroring009,Part__Feature017,Part__Mirroring010,+16 more]
  License = CC BY 3.0
  LicenseURL = http://creativecommons.org/licenses/by/3.0/
  Origin = -> Origin005
  Placement = pos=(-17.2,-26.2,15) rot=(1,0,0;4.71239rad)
FEATURE [Part::Feature] Fusion001  label="E3DV6_Assembly"
  Placement = pos=(-35.0897,-39.6601,8.5) rot=(0,0.707107,0.707107;3.14159rad)
  shape: bbox 27.55 x 22.3 x 63.4 mm, 442 faces, 3 solids (baked)
FEATURE [PartDesign::Plane] DatumPlane020  label="Überhang_X_Tisch_TitanHalter"
  AttachmentOffset = pos=(0,0,4) rot=(0,0,1;0rad)
  Length = 30.3498
  MapMode = 11
  Placement = pos=(4,-11,1.6934e-12) rot=(0.707107,0,0.707107;3.14159rad)
  ResizeMode = 0
  Support = -> [Sketch]
  Width = 48.3498
FEATURE [PartDesign::Pad] Pad005  label="Überhang_Zu_FanWand"
  BaseFeature = -> Pocket007003
  Length = 4
  Length2 = 100
  Placement = pos=(0,0,0) rot=(1,0,0;1.5708rad)
  Profile = -> Sketch012
  Reversed = true
  Type = 3
  UpToFace = -> DatumPlane020 [Plane]
FEATURE [Sketcher::SketchObject] Sketch018
  ExternalGeometry = -> [DatumPlane020]
  MapMode = 5
  Placement = pos=(-2.8207e-12,-11,14) rot=(0,0,-1;1.5708rad)
  Support = -> [DatumPlane002]
  expr: Constraints[8] = 2 * BaseDimensions.Constraints.Radius_Aussen_Achsenlagerkörper
  sketch-geometry (4):
    g0: LineSegment StartX=-11 StartY=4 StartZ=0 EndX=11 EndY=4 EndZ=0
    g1: LineSegment StartX=11 StartY=4 StartZ=0 EndX=11 EndY=2 EndZ=0
    g2: LineSegment StartX=11 StartY=2 StartZ=0 EndX=-11 EndY=2 EndZ=0
    g3: LineSegment StartX=-11 StartY=2 StartZ=0 EndX=-11 EndY=4 EndZ=0
  constraints (11):
    c: Coincident(g0,g1)
    c: Coincident(g1,g2)
    c: Coincident(g2,g3)
    c: Coincident(g3,g0)
    c: Horizontal(g0)
    c: Vertical(g1)
    c: Vertical(g3)
    c: Symmetric(g2,g1,g-2)
    c: DistanceX(g2,g2) = 22
    c: DistanceY(g1,g1) = 2  'Dicke_Lüfterwand'
    c: PointOnObject(g0,g-3)
FEATURE [PartDesign::Plane] DatumPlane021  label="Überhang_X_Tisch_TitanHalter2"
  AttachmentOffset = pos=(0,0,52) rot=(0,0,1;0rad)
  Length = 48.3498
  MapMode = 2
  Placement = pos=(-52,5.8771e-12,-5.8771e-12) rot=(-0.57735,0.57735,0.57735;4.18879rad)
  ResizeMode = 0
  Support = -> [Sketch]
  Width = 30.3498
  expr: AttachmentOffset.Base.z = 2 * BaseDimensions.Constraints.Length_IgusBearing + 4mm
FEATURE [PartDesign::Pad] Pad006  label="Überhang_Zu_FanWand2"
  BaseFeature = -> Pad005
  Length = 4
  Length2 = 100
  Placement = pos=(0,0,0) rot=(1,0,0;1.5708rad)
  Profile = -> Sketch013
  Type = 3
  UpToFace = -> DatumPlane021
FEATURE [PartDesign::Pad] Pad007  label="Lüfterwand1"
  BaseFeature = -> Pad006
  Length = 15
  Length2 = 100
  Placement = pos=(0,0,0) rot=(1,0,0;1.5708rad)
  Profile = -> Sketch018
  Type = 0
  expr: Length = BaseDimensions.Constraints.Höhe_Lüfterwand
FEATURE [Sketcher::SketchObject] Sketch019
  ExternalGeometry = -> [DatumPlane004,DatumPlane021]
  MapMode = 5
  Placement = pos=(-2.8207e-12,-11,14) rot=(0,0,-1;1.5708rad)
  Support = -> [DatumPlane002]
  expr: Constraints[8] = Sketch018.Constraints.Dicke_Lüfterwand
  expr: Constraints[9] = 2 * BaseDimensions.Constraints.Radius_Aussen_Achsenlagerkörper
  sketch-geometry (4):
    g0: LineSegment StartX=-11 StartY=-50 StartZ=0 EndX=11 EndY=-50 EndZ=0
    g1: LineSegment StartX=11 StartY=-50 StartZ=0 EndX=11 EndY=-52 EndZ=0
    g2: LineSegment StartX=11 StartY=-52 StartZ=0 EndX=-11 EndY=-52 EndZ=0
    g3: LineSegment StartX=-11 StartY=-52 StartZ=0 EndX=-11 EndY=-50 EndZ=0
  constraints (11):
    c: Coincident(g0,g1)
    c: Coincident(g1,g2)
    c: Coincident(g2,g3)
    c: Coincident(g3,g0)
    c: Horizontal(g2)
    c: Vertical(g1)
    c: Vertical(g3)
    c: Symmetric(g0,g0,g-2)
    c: DistanceY(g1,g1) = 2
    c: DistanceX(g2,g2) = 22
    c: PointOnObject(g1,g-4)
FEATURE [PartDesign::Pad] Pad008  label="Lüfeterwand2"
  BaseFeature = -> Pad007
  Length = 15
  Length2 = 100
  Placement = pos=(0,0,0) rot=(1,0,0;1.5708rad)
  Profile = -> Sketch019
  Type = 0
  expr: Length = BaseDimensions.Constraints.Höhe_Lüfterwand
FEATURE [Sketcher::SketchObject] Sketch023
  ExternalGeometry = -> [DatumPlane004,DatumPlane020,DatumPlane021]
  MapMode = 5
  Placement = pos=(-2.8207e-12,-11,14) rot=(0,0,-1;1.5708rad)
  Support = -> [DatumPlane002]
  expr: Constraints[6] = Sketch018.Constraints.Dicke_Lüfterwand
  sketch-geometry (4):
    g0: LineSegment StartX=-40 StartY=2 StartZ=0 EndX=40 EndY=2 EndZ=0
    g1: LineSegment StartX=40 StartY=2 StartZ=0 EndX=40 EndY=-50 EndZ=0
    g2: LineSegment StartX=40 StartY=-50 StartZ=0 EndX=-40 EndY=-50 EndZ=0
    g3: LineSegment StartX=-40 StartY=-50 StartZ=0 EndX=-40 EndY=2 EndZ=0
  constraints (10):
    c: Coincident(g0,g1)
    c: Coincident(g1,g2)
    c: Coincident(g2,g3)
    c: Coincident(g3,g0)
    c: Horizontal(g2)
    c: Vertical(g3)
    c: Distance(g0,g-4) = 2
    c: Symmetric(g0,g1,g-3)
    c: DistanceX(g0,g0) = 80  '80'
    c: Symmetric(g0,g0,g-2)
FEATURE [Sketcher::SketchObject] Sketch051
  ExternalGeometry = -> [DatumPlane002]
  MapMode = 5
  Placement = pos=(4,-11,1.6934e-12) rot=(0.707107,0,0.707107;3.14159rad)
  Support = -> [DatumPlane020]
  expr: Constraints[9] = BaseDimensions.Constraints.Radius_Aussen_Achsenlagerkörper + BaseDimensions.Constraints.Länge_Überhang_FanTisch
  expr: Constraints[8] = BaseDimensions.Constraints.Radius_Aussen_Achsenlagerkörper
  sketch-geometry (4):
    g0: LineSegment StartX=17 StartY=21 StartZ=0 EndX=20 EndY=21 EndZ=0
    g1: LineSegment StartX=20 StartY=21 StartZ=0 EndX=20 EndY=-11 EndZ=0
    g2: LineSegment StartX=20 StartY=-11 StartZ=0 EndX=17 EndY=-11 EndZ=0
    g3: LineSegment StartX=17 StartY=-11 StartZ=0 EndX=17 EndY=21 EndZ=0
  constraints (12):
    c: Coincident(g0,g1)
    c: Coincident(g1,g2)
    c: Coincident(g2,g3)
    c: Coincident(g3,g0)
    c: Horizontal(g0)
    c: Horizontal(g2)
    c: Vertical(g1)
    c: Vertical(g3)
    c: DistanceY(g1,g-1) = 11
    c: DistanceY(g-1,g0) = 21
    c: Distance(g2,g-3) = 3
    c: DistanceX(g2,g1) = 3
FEATURE [PartDesign::Pad] Pad025  label="Lüftermountingtisch1"
  BaseFeature = -> Pad008
  Length = 23.5
  Length2 = 100
  Placement = pos=(0,0,0) rot=(1,0,0;1.5708rad)
  Profile = -> Sketch051
  Type = 0
  expr: Length = BaseDimensions.Constraints.Länge_FanTisch
FEATURE [Sketcher::SketchObject] Sketch052
  ExternalGeometry = -> [DatumPlane003]
  MapMode = 5
  Placement = pos=(-2.8207e-12,-11,14) rot=(0,0,-1;1.5708rad)
  Support = -> [DatumPlane002]
  expr: Constraints[6] = BaseDimensions.Constraints.Radius_Einpresshülse
  sketch-geometry (6):
    g0: LineSegment [constr] StartX=17 StartY=24 StartZ=0 EndX=17 EndY=0 EndZ=0
    g1: Circle CenterX=17 CenterY=9 CenterZ=0 NormalX=0 NormalY=0 NormalZ=1 AngleXU=0 Radius=1.85
    g2: Circle CenterX=17 CenterY=24 CenterZ=0 NormalX=0 NormalY=0 NormalZ=1 AngleXU=0 Radius=1.85
    g3: LineSegment [constr] StartX=17 StartY=24 StartZ=0 EndX=-5 EndY=24 EndZ=0
    g4: Circle CenterX=5 CenterY=24 CenterZ=0 NormalX=0 NormalY=0 NormalZ=1 AngleXU=0 Radius=1.85
    g5: Circle CenterX=-5 CenterY=24 CenterZ=0 NormalX=0 NormalY=0 NormalZ=1 AngleXU=0 Radius=1.85
  constraints (17):
    c: Vertical(g0)
    c: PointOnObject(g0,g-1)
    c: Distance(g0,g-3) = 6
    c: PointOnObject(g1,g0)
    c: DistanceY(g0,g1) = 9
    c: DistanceY(g1,g2) = 15
    c: Radius(g1) = 1.85
    c: Equal(g1,g2)
    c: Coincident(g0,g2)
    c: Coincident(g3,g0)
    c: Horizontal(g3)
    c: DistanceX(g3,g0) = 22
    c: PointOnObject(g4,g3)
    c: DistanceX(g3,g4) = 10
    c: Coincident(g5,g3)
    c: Equal(g2,g4)
    c: Equal(g5,g4)
FEATURE [Sketcher::SketchObject] Sketch027  label="Inteface_To_Fans"
  ExternalGeometry = -> [Sketch052,DatumPlane004,DatumPlane005,DatumPlane020,DatumPlane021]
  MapMode = 5
  Placement = pos=(-2.8207e-12,-11,14) rot=(0,0,-1;1.5708rad)
  Support = -> [DatumPlane002]
  expr: Constraints[39] = Lüftermountingtisch1.Length
  expr: Constraints[36] = 2 * BaseDimensions.Constraints.Radius_Aussen_Achsenlagerkörper + BaseDimensions.Constraints.Länge_Überhang_FanTisch
  expr: Constraints[0] = BaseDimensions.Constraints.Radius_Einpresshülse
  sketch-geometry (16):
    g0: Circle CenterX=-5 CenterY=24 CenterZ=0 NormalX=0 NormalY=0 NormalZ=1 AngleXU=0 Radius=1.85
    g1: Circle CenterX=5 CenterY=24 CenterZ=0 NormalX=0 NormalY=0 NormalZ=1 AngleXU=0 Radius=1.85
    g2: Circle CenterX=17 CenterY=24 CenterZ=0 NormalX=0 NormalY=0 NormalZ=1 AngleXU=0 Radius=1.85
    g3: Circle CenterX=17 CenterY=9 CenterZ=0 NormalX=0 NormalY=0 NormalZ=1 AngleXU=0 Radius=1.85
    g4: Circle CenterX=-5 CenterY=-72 CenterZ=0 NormalX=0 NormalY=0 NormalZ=1 AngleXU=0 Radius=1.85
    g5: Circle CenterX=5 CenterY=-72 CenterZ=0 NormalX=0 NormalY=0 NormalZ=1 AngleXU=0 Radius=1.85
    g6: Circle CenterX=17 CenterY=-72 CenterZ=0 NormalX=0 NormalY=0 NormalZ=1 AngleXU=0 Radius=1.85
    g7: Circle CenterX=17 CenterY=-57 CenterZ=0 NormalX=0 NormalY=0 NormalZ=1 AngleXU=0 Radius=1.85
    g8: LineSegment StartX=-11 StartY=-75.5 StartZ=0 EndX=21 EndY=-75.5 EndZ=0
    g9: LineSegment StartX=21 StartY=-75.5 StartZ=0 EndX=21 EndY=-52 EndZ=0
    g10: LineSegment StartX=21 StartY=-52 StartZ=0 EndX=-11 EndY=-52 EndZ=0
    g11: LineSegment StartX=-11 StartY=-52 StartZ=0 EndX=-11 EndY=-75.5 EndZ=0
    g12: LineSegment StartX=-11 StartY=27.5 StartZ=0 EndX=21 EndY=27.5 EndZ=0
    g13: LineSegment StartX=21 StartY=27.5 StartZ=0 EndX=21 EndY=4 EndZ=0
    g14: LineSegment StartX=21 StartY=4 StartZ=0 EndX=-11 EndY=4 EndZ=0
    g15: LineSegment StartX=-11 StartY=4 StartZ=0 EndX=-11 EndY=27.5 EndZ=0
  constraints (34):
    c: Radius(g0) = 1.85
    c: Equal(g0, g1-g7) x7
    c: Coincident(g8,g9)
    c: Coincident(g9,g10)
    c: Coincident(g10,g11)
    c: Coincident(g11,g8)
    c: Horizontal(g8)
    c: Horizontal(g10)
    c: Vertical(g9)
    c: Vertical(g11)
    c: Coincident(g12,g13)
    c: Coincident(g13,g14)
    c: Coincident(g14,g15)
    c: Coincident(g15,g12)
    c: Horizontal(g12)
    c: Horizontal(g14)
    c: Vertical(g13)
    c: Vertical(g15)
    c: PointOnObject(g13,g9)
    c: Coincident(g2,g-3)
    c: Coincident(g3,g-6)
    c: Coincident(g1,g-4)
    c: Coincident(g0,g-5)
    c: Symmetric(g3,g7,g-7)
    c: Symmetric(g6,g2,g-7)
    c: Symmetric(g5,g1,g-7)
    c: Symmetric(g4,g0,g-7)
    c: PointOnObject(g13,g-9)
    c: PointOnObject(g14,g-8)
    c: PointOnObject(g9,g-10)
    c: DistanceX(g12,g12) = 32
    c: Equal(g12,g8)
    c: Equal(g13,g9)
    c: DistanceY(g13,g13) = 23.5
FEATURE [PartDesign::ShapeBinder] ShapeBinder
  Placement = pos=(-2.821e-12,-11,14) rot=(0,0,-1;1.5708rad)
  Support = -> [Sketch027]
  TraceSupport = false
FEATURE [Sketcher::SketchObject] Sketch028
  ExternalGeometry = -> [ShapeBinder]
  MapMode = 5
  Support = -> [XY_Plane001]
  sketch-geometry (14):
    g0: Circle CenterX=-72 CenterY=-28 CenterZ=0 NormalX=0 NormalY=0 NormalZ=1 AngleXU=0 Radius=2.25
    g1: Circle CenterX=-72 CenterY=-16 CenterZ=0 NormalX=0 NormalY=0 NormalZ=1 AngleXU=0 Radius=2.25
    g2: Circle CenterX=-72 CenterY=-6 CenterZ=0 NormalX=0 NormalY=0 NormalZ=1 AngleXU=0 Radius=2.25
    g3: LineSegment StartX=-52 StartY=-32 StartZ=0 EndX=-75.5 EndY=-32 EndZ=0
    g4: LineSegment StartX=-75.5 StartY=-32 StartZ=0 EndX=-75.5 EndY=6.0005e-12 EndZ=0
    g5: LineSegment StartX=-75.5 StartY=6e-12 StartZ=0 EndX=-54 EndY=6e-12 EndZ=0
    g6: LineSegment StartX=-62 StartY=-7.01066 StartZ=0 EndX=-57 EndY=-7.01066 EndZ=0
    g7: LineSegment StartX=-57 StartY=-7.01066 StartZ=0 EndX=-57 EndY=-22.0107 EndZ=0
    g8: LineSegment StartX=-57 StartY=-22.0107 StartZ=0 EndX=-62 EndY=-22.0107 EndZ=0
    g9: LineSegment StartX=-62 StartY=-22.0107 StartZ=0 EndX=-62 EndY=-7.01066 EndZ=0
    g10: LineSegment StartX=-52 StartY=-32 StartZ=0 EndX=-52 EndY=-23.0107 EndZ=0
    g11: LineSegment StartX=-52 StartY=-23.0107 StartZ=0 EndX=-54 EndY=-23.0107 EndZ=0
    g12: LineSegment StartX=-54 StartY=-23.0107 StartZ=0 EndX=-54 EndY=6.0005e-12 EndZ=0
    g13: Circle CenterX=-57 CenterY=-28 CenterZ=0 NormalX=0 NormalY=0 NormalZ=1 AngleXU=0 Radius=2.25
  constraints (36):
    c: Coincident(g0,g-5)
    c: Coincident(g1,g-4)
    c: Coincident(g2,g-3)
    c: Radius(g0) = 2.25
    c: Equal(g0,g1)
    c: Equal(g0,g2)
    c: Coincident(g3,g4)
    c: Coincident(g4,g5)
    c: Horizontal(g3)
    c: Horizontal(g5)
    c: Vertical(g4)
    c: Coincident(g3,g-9)
    c: PointOnObject(g5,g-8)
    c: Coincident(g6,g7)
    c: Coincident(g7,g8)
    c: Coincident(g8,g9)
    c: Coincident(g9,g6)
    c: Horizontal(g6)
    c: Horizontal(g8)
    c: Vertical(g7)
    c: Vertical(g9)
    c: DistanceY(g7,g7) = 15
    c: DistanceX(g7,g-7) = 5
    c: DistanceX(g8,g8) = 5
    c: Coincident(g3,g10)
    c: Vertical(g10)
    c: Coincident(g10,g11)
    c: Horizontal(g11)
    c: Coincident(g11,g12)
    c: Vertical(g12)
    c: Coincident(g5,g12)
    c: Coincident(g-7,g3)
    c: DistanceX(g11,g11) = 2
    c: DistanceY(g11,g7) = 1
    c: Coincident(g13,g-6)
    c: Equal(g13,g0)
FEATURE [PartDesign::Pad] Pad012
  Length = 2
  Length2 = 100
  Profile = -> Sketch028
  Type = 0
FEATURE [Sketcher::SketchObject] Sketch029
  ExternalGeometry = -> [ShapeBinder]
  MapMode = 5
  Support = -> [XY_Plane001]
  sketch-geometry (4):
    g0: LineSegment StartX=-67.65 StartY=-1.75 StartZ=0 EndX=-70.15 EndY=-1.75 EndZ=0
    g1: LineSegment StartX=-70.15 StartY=-1.75 StartZ=0 EndX=-70.15 EndY=27.714 EndZ=0
    g2: LineSegment StartX=-70.15 StartY=27.714 StartZ=0 EndX=-67.65 EndY=27.714 EndZ=0
    g3: LineSegment StartX=-67.65 StartY=27.714 StartZ=0 EndX=-67.65 EndY=-1.75 EndZ=0
  constraints (11):
    c: Coincident(g0,g1)
    c: Coincident(g1,g2)
    c: Coincident(g2,g3)
    c: Coincident(g3,g0)
    c: Horizontal(g0)
    c: Horizontal(g2)
    c: Vertical(g1)
    c: Vertical(g3)
    c: DistanceX(g2,g2) = 2.5
    c: DistanceX(g-3,g0) = 5.35
    c: DistanceY(g-3,g0) = -1.75
FEATURE [PartDesign::Pad] Pad013
  BaseFeature = -> Pad012
  Length = 16
  Length2 = 100
  Profile = -> Sketch029
  Type = 0
FEATURE [PartDesign::Plane] DatumPlane006
  AttachmentOffset = pos=(0,0,0) rot=(0,1,0;1.5708rad)
  Length = 67.5946
  MapMode = 7
  Placement = pos=(-70.15,-1.75,0) rot=(0.57735,0.57735,0.57735;2.0944rad)
  ResizeMode = 0
  Support = -> [Sketch029]
  Width = 33.8805
FEATURE [Sketcher::SketchObject] Sketch030
  MapMode = 5
  Placement = pos=(-70.15,-1.75,0) rot=(0.57735,0.57735,0.57735;2.0944rad)
  Support = -> [DatumPlane006]
  sketch-geometry (1):
    g0: Circle CenterX=24.4148 CenterY=10.9837 CenterZ=0 NormalX=0 NormalY=0 NormalZ=1 AngleXU=0 Radius=2.5
  constraints (1):
    c: Radius(g0) = 2.5
FEATURE [PartDesign::Pocket] Pocket007005
  BaseFeature = -> Pad013
  Length = 5
  Length2 = 100
  Profile = -> Sketch030
  Reversed = true
  Type = 1
FEATURE [PartDesign::Plane] DatumPlane007
  AttachmentOffset = pos=(0,0,0) rot=(0,1,0;1.5708rad)
  Length = 94.9297
  MapMode = 7
  Placement = pos=(-52,-32,0) rot=(0,0.707107,0.707107;3.14159rad)
  ResizeMode = 0
  Support = -> [Sketch028]
  Width = 35.4297
FEATURE [PartDesign::ShapeBinder] ShapeBinder001
  Placement = pos=(-2.821e-12,-11,14) rot=(0,0,-1;1.5708rad)
  Support = -> [Sketch027]
  TraceSupport = false
FEATURE [Sketcher::SketchObject] Sketch036
  ExternalGeometry = -> [ShapeBinder001]
  MapMode = 5
  Support = -> [XY_Plane002]
  sketch-geometry (9):
    g0: Circle CenterX=-72 CenterY=-16 CenterZ=0 NormalX=0 NormalY=0 NormalZ=1 AngleXU=0 Radius=2.25
    g1: Circle CenterX=-72 CenterY=-28 CenterZ=0 NormalX=0 NormalY=0 NormalZ=1 AngleXU=0 Radius=2.25
    g2: Circle CenterX=-57 CenterY=-28 CenterZ=0 NormalX=0 NormalY=0 NormalZ=1 AngleXU=0 Radius=2.25
    g3: LineSegment StartX=-75.5 StartY=-11 StartZ=0 EndX=-68 EndY=-11 EndZ=0
    g4: LineSegment StartX=-68 StartY=-11 StartZ=0 EndX=-68 EndY=-22.5 EndZ=0
    g5: LineSegment StartX=-68 StartY=-22.5 StartZ=0 EndX=-52 EndY=-22.5 EndZ=0
    g6: LineSegment StartX=-52 StartY=-22.5 StartZ=0 EndX=-52 EndY=-32 EndZ=0
    g7: LineSegment StartX=-52 StartY=-32 StartZ=0 EndX=-75.5 EndY=-32 EndZ=0
    g8: LineSegment StartX=-75.5 StartY=-32 StartZ=0 EndX=-75.5 EndY=-11 EndZ=0
  constraints (21):
    c: Coincident(g0,g-4)
    c: Coincident(g1,g-5)
    c: Coincident(g2,g-6)
    c: Radius(g1) = 2.25
    c: Equal(g1,g0)
    c: Equal(g1,g2)
    c: PointOnObject(g3,g-7)
    c: Coincident(g3,g4)
    c: Vertical(g4)
    c: Coincident(g4,g5)
    c: Horizontal(g5)
    c: Coincident(g5,g6)
    c: Vertical(g6)
    c: Coincident(g6,g7)
    c: Coincident(g7,g8)
    c: Coincident(g8,g3)
    c: Symmetric(g0,g-3,g3)
    c: Coincident(g7,g-9)
    c: Coincident(g6,g-10)
    c: DistanceX(g5,g5) = 16
    c: Distance(g6) = 9.5  'FrontPartLength'
FEATURE [PartDesign::Pad] Pad016
  Length = 2.25
  Length2 = 100
  Profile = -> Sketch036
  Type = 0
FEATURE [PartDesign::Plane] DatumPlane009
  AttachmentOffset = pos=(0,0,0) rot=(0,1,0;1.5708rad)
  Length = 112.944
  MapMode = 7
  Placement = pos=(-68,-22.5,0) rot=(1,0,0;1.5708rad)
  ResizeMode = 0
  Support = -> [Sketch036]
  Width = 33.9438
FEATURE [Sketcher::SketchObject] Sketch037
  ExternalGeometry = -> [Sketch036]
  MapMode = 5
  Placement = pos=(-68,-22.5,0) rot=(1,0,0;1.5708rad)
  Support = -> [DatumPlane009]
  sketch-geometry (4):
    g0: LineSegment StartX=14 StartY=2.25 StartZ=0 EndX=3 EndY=2.25 EndZ=0
    g1: LineSegment StartX=3 StartY=2.25 StartZ=0 EndX=3 EndY=1.25 EndZ=0
    g2: LineSegment StartX=3 StartY=1.25 StartZ=0 EndX=14 EndY=1.25 EndZ=0
    g3: LineSegment StartX=14 StartY=1.25 StartZ=0 EndX=14 EndY=2.25 EndZ=0
  constraints (12):
    c: Coincident(g0,g1)
    c: Coincident(g1,g2)
    c: Coincident(g2,g3)
    c: Coincident(g3,g0)
    c: Horizontal(g0)
    c: Horizontal(g2)
    c: Vertical(g1)
    c: Vertical(g3)
    c: DistanceY(g-3,g2) = 1.25
    c: DistanceY(g3,g3) = 1
    c: DistanceX(g0,g0) = 11
    c: DistanceX(g2,g-3) = 2
FEATURE [PartDesign::Pad] Pad017
  BaseFeature = -> Pad016
  Length = 10
  Length2 = 100
  Profile = -> Sketch037
  Reversed = true
  Type = 0
FEATURE [PartDesign::Plane] DatumPlane010
  AttachmentOffset = pos=(0,0,2.25) rot=(0,0,1;0rad)
  Length = 116.154
  MapMode = 2
  Placement = pos=(0,0,2.25) rot=(0,0,1;0rad)
  ResizeMode = 0
  Support = -> [Sketch036]
  Width = 55.1545
  expr: AttachmentOffset.Base.z = Pad016.Length
FEATURE [Sketcher::SketchObject] Sketch038
  ExternalGeometry = -> [Sketch036]
  MapMode = 5
  Placement = pos=(0,0,2.25) rot=(0,0,1;0rad)
  Support = -> [DatumPlane010]
  sketch-geometry (4):
    g0: LineSegment StartX=-67.25 StartY=-22.5 StartZ=0 EndX=-52 EndY=-22.5 EndZ=0
    g1: LineSegment StartX=-52 StartY=-22.5 StartZ=0 EndX=-52 EndY=-32 EndZ=0
    g2: LineSegment StartX=-52 StartY=-32 StartZ=0 EndX=-67.25 EndY=-32 EndZ=0
    g3: LineSegment StartX=-67.25 StartY=-32 StartZ=0 EndX=-67.25 EndY=-22.5 EndZ=0
  constraints (12):
    c: Coincident(g0,g1)
    c: Coincident(g1,g2)
    c: Coincident(g2,g3)
    c: Coincident(g3,g0)
    c: Horizontal(g0)
    c: Horizontal(g2)
    c: Vertical(g1)
    c: Vertical(g3)
    c: PointOnObject(g0,g-3)
    c: PointOnObject(g1,g-4)
    c: DistanceX(g-3,g0) = 0.75
    c: DistanceX(g0,g-3) = 0
FEATURE [PartDesign::Pad] Pad018
  BaseFeature = -> Pad017
  Length = 17.25
  Length2 = 100
  Profile = -> Sketch038
  Type = 0
  expr: Length = 19.5mm - Pad016.Length
FEATURE [Sketcher::SketchObject] Sketch039
  ExternalGeometry = -> [Sketch038]
  MapMode = 5
  Placement = pos=(-68,-22.5,0) rot=(1,0,0;1.5708rad)
  Support = -> [DatumPlane009]
  expr: Constraints[11] = Pad018.Length - Sketch039.Constraints.WallThickness
  expr: Constraints[10] = Sketch039.Constraints.WallThickness + 0.5mm
  sketch-geometry (4):
    g0: LineSegment StartX=2.25 StartY=2.25 StartZ=0 EndX=14 EndY=2.25 EndZ=0
    g1: LineSegment StartX=14 StartY=2.25 StartZ=0 EndX=14 EndY=18 EndZ=0
    g2: LineSegment StartX=14 StartY=18 StartZ=0 EndX=2.25 EndY=18 EndZ=0
    g3: LineSegment StartX=2.25 StartY=18 StartZ=0 EndX=2.25 EndY=2.25 EndZ=0
  constraints (12):
    c: Coincident(g0,g1)
    c: Coincident(g1,g2)
    c: Coincident(g2,g3)
    c: Coincident(g3,g0)
    c: Horizontal(g0)
    c: Horizontal(g2)
    c: Vertical(g1)
    c: Vertical(g3)
    c: PointOnObject(g0,g-5)
    c: DistanceX(g-5,g0) = 1.5  'WallThickness'
    c: DistanceX(g0,g-5) = 2
    c: DistanceY(g3,g3) = 15.75
FEATURE [PartDesign::Pocket] Pocket007008
  BaseFeature = -> Pad018
  Length = 5
  Length2 = 100
  Profile = -> Sketch039
  Reversed = true
  Type = 1
FEATURE [PartDesign::Plane] DatumPlane011
  AttachmentOffset = pos=(0,0,0) rot=(0,1,0;1.5708rad)
  Length = 48.3498
  MapMode = 45
  Placement = pos=(-52,-27.25,2.25) rot=(-0.57735,0.57735,0.57735;4.18879rad)
  ResizeMode = 0
  Support = -> [Sketch038]
  Width = 30.3498
FEATURE [Sketcher::SketchObject] Sketch040
  MapMode = 5
  Placement = pos=(-52,-27.25,2.25) rot=(0.57735,-0.57735,-0.57735;2.0944rad)
  Support = -> [DatumPlane011]
  expr: Constraints[1] = Pad018.Length / 2
  sketch-geometry (1):
    g0: Circle CenterX=0 CenterY=8.625 CenterZ=0 NormalX=0 NormalY=0 NormalZ=1 AngleXU=0 Radius=1
  constraints (3):
    c: PointOnObject(g0,g-2)
    c: DistanceY(g-1,g0) = 8.625
    c: Radius(g0) = 1
FEATURE [PartDesign::Pocket] Pocket007009
  BaseFeature = -> Pocket007008
  Length = 5
  Length2 = 100
  Profile = -> Sketch040
  Reversed = true
  Type = 1
FEATURE [PartDesign::Plane] DatumPlane012
  AttachmentOffset = pos=(0,0,0) rot=(0,1,0;1.5708rad)
  Length = 67.5946
  MapMode = 7
  Placement = pos=(-70.15,-1.75,0) rot=(0.57735,0.57735,0.57735;2.0944rad)
  ResizeMode = 0
  Support = -> [Sketch029]
  Width = 33.8805
FEATURE [Sketcher::SketchObject] Sketch041
  MapMode = 5
  Placement = pos=(-70.15,-1.75,0) rot=(0.57735,0.57735,0.57735;2.0944rad)
  Support = -> [DatumPlane012]
  sketch-geometry (3):
    g0: LineSegment StartX=-2.3261 StartY=2.49481 StartZ=0 EndX=28.9441 EndY=20.4569 EndZ=0
    g1: LineSegment StartX=28.9441 StartY=20.4569 StartZ=0 EndX=-2.3261 EndY=20.4569 EndZ=0
    g2: LineSegment StartX=-2.3261 StartY=20.4569 StartZ=0 EndX=-2.3261 EndY=2.49481 EndZ=0
  constraints (6):
    c: PointOnObject(g1,g0)
    c: Coincident(g1,g2)
    c: Coincident(g0,g2)
    c: Vertical(g2)
    c: Horizontal(g1)
    c: Coincident(g0,g1)
FEATURE [PartDesign::Pocket] Pocket007010
  BaseFeature = -> Pocket007005
  Length = 5
  Length2 = 100
  Profile = -> Sketch041
  Reversed = true
  Type = 0
FEATURE [PartDesign::Body] Body001  label="Left-Fan-Clamp1-design"
  Group = -> [ShapeBinder,Sketch028,Pad012,Sketch029,Pad013,DatumPlane006,Sketch030,Pocket007005,DatumPlane007,DatumPlane012,Sketch041,Pocket007010]
  Origin = -> Origin001
  Placement = pos=(0,0,20) rot=(0,0,1;0rad)
  Tip = -> Pocket007010
FEATURE [PartDesign::Plane] DatumPlane013
  Length = 112.944
  MapMode = 2
  Placement = pos=(-68,-22.5,0) rot=(1,0,0;1.5708rad)
  ResizeMode = 0
  Support = -> [Sketch039]
  Width = 33.9438
FEATURE [Sketcher::SketchObject] Sketch042
  ExternalGeometry = -> [Sketch039]
  MapMode = 5
  Placement = pos=(-68,-22.5,0) rot=(1,0,0;1.5708rad)
  Support = -> [DatumPlane013]
  expr: Constraints[21] = Sketch042.Constraints.WallThickness
  expr: Constraints[20] = Sketch042.Constraints.WallThickness
  sketch-geometry (8):
    g0: LineSegment StartX=14.5 StartY=18.5 StartZ=0 EndX=14.5 EndY=2.25 EndZ=0
    g1: LineSegment StartX=1.75 StartY=2.25 StartZ=0 EndX=1.75 EndY=18.5 EndZ=0
    g2: LineSegment StartX=14 StartY=18 StartZ=0 EndX=14 EndY=2.25 EndZ=0
    g3: LineSegment StartX=2.25 StartY=2.25 StartZ=0 EndX=2.25 EndY=18 EndZ=0
    g4: LineSegment StartX=1.75 StartY=2.25 StartZ=0 EndX=2.25 EndY=2.25 EndZ=0
    g5: LineSegment StartX=14 StartY=2.25 StartZ=0 EndX=14.5 EndY=2.25 EndZ=0
    g6: LineSegment StartX=1.75 StartY=18.5 StartZ=0 EndX=14.5 EndY=18.5 EndZ=0
    g7: LineSegment StartX=2.25 StartY=18 StartZ=0 EndX=14 EndY=18 EndZ=0
  constraints (23):
    c: Vertical(g0)
    c: Vertical(g1)
    c: Vertical(g2)
    c: Vertical(g3)
    c: PointOnObject(g-4,g2)
    c: Coincident(g4,g1)
    c: Coincident(g4,g3)
    c: Horizontal(g4)
    c: Coincident(g5,g2)
    c: Coincident(g5,g0)
    c: Horizontal(g5)
    c: DistanceY(g2,g-4) = 0
    c: DistanceY(g3,g-5) = 0
    c: Coincident(g6,g1)
    c: Coincident(g6,g0)
    c: Horizontal(g6)
    c: Coincident(g7,g3)
    c: Coincident(g7,g2)
    c: Horizontal(g7)
    c: DistanceX(g1,g3) = 0.5  'WallThickness'
    c: DistanceX(g2,g0) = 0.5
    c: DistanceY(g2,g0) = 0.5
    c: Coincident(g3,g-5)
FEATURE [PartDesign::Pad] Pad019
  BaseFeature = -> Pocket007009
  Length = 5
  Length2 = 100
  Profile = -> Sketch042
  Reversed = true
  Type = 0
FEATURE [PartDesign::Plane] DatumPlane014
  AttachmentOffset = pos=(0,0,5) rot=(0,0,1;0rad)
  Length = 112.944
  MapMode = 2
  Placement = pos=(-68,-17.5,1.1e-15) rot=(0,0.707107,0.707107;3.14159rad)
  ResizeMode = 0
  Support = -> [Sketch042]
  Width = 33.9438
  expr: AttachmentOffset.Base.z = Pad019.Length
FEATURE [Sketcher::SketchObject] Sketch043
  ExternalGeometry = -> [Sketch042]
  MapMode = 5
  Placement = pos=(-68,-17.5,1.1e-15) rot=(0,0.707107,0.707107;3.14159rad)
  Support = -> [DatumPlane014]
  sketch-geometry (4):
    g0: LineSegment StartX=-14.5 StartY=18.5 StartZ=0 EndX=-13.5 EndY=18.5 EndZ=0
    g1: LineSegment StartX=-13.5 StartY=18.5 StartZ=0 EndX=-13.5 EndY=11.5 EndZ=0
    g2: LineSegment StartX=-13.5 StartY=11.5 StartZ=0 EndX=-14.5 EndY=11.5 EndZ=0
    g3: LineSegment StartX=-14.5 StartY=11.5 StartZ=0 EndX=-14.5 EndY=18.5 EndZ=0
  constraints (11):
    c: Coincident(g0,g1)
    c: Coincident(g1,g2)
    c: Coincident(g2,g3)
    c: Coincident(g3,g0)
    c: Horizontal(g0)
    c: Horizontal(g2)
    c: Vertical(g1)
    c: Vertical(g3)
    c: Coincident(g0,g-3)
    c: DistanceX(g0,g0) = 1
    c: DistanceY(g3,g3) = 7
FEATURE [PartDesign::Pocket] Pocket007011
  BaseFeature = -> Pad019
  Length = 3
  Length2 = 100
  Profile = -> Sketch043
  Type = 0
  expr: Length = Pad019.Length - 2mm
FEATURE [PartDesign::Plane] DatumPlane015
  AttachmentOffset = pos=(0,0,9.5) rot=(0,0,1;0rad)
  Length = 112.944
  MapMode = 2
  Placement = pos=(-68,-32,-2.1e-15) rot=(1,0,0;1.5708rad)
  ResizeMode = 0
  Support = -> [Sketch039]
  Width = 33.9438
  expr: AttachmentOffset.Base.z = Sketch036.Constraints.FrontPartLength
FEATURE [Sketcher::SketchObject] Sketch044  label="InterfaceToFanDuct"
  ExternalGeometry = -> [Sketch039]
  MapMode = 5
  Placement = pos=(-68,-32,-2.1e-15) rot=(1,0,0;1.5708rad)
  Support = -> [DatumPlane015]
  sketch-geometry (4):
    g0: LineSegment StartX=2.25 StartY=18 StartZ=0 EndX=14 EndY=18 EndZ=0
    g1: LineSegment StartX=14 StartY=18 StartZ=0 EndX=14 EndY=2.25 EndZ=0
    g2: LineSegment StartX=14 StartY=2.25 StartZ=0 EndX=2.25 EndY=2.25 EndZ=0
    g3: LineSegment StartX=2.25 StartY=2.25 StartZ=0 EndX=2.25 EndY=18 EndZ=0
  constraints (10):
    c: Coincident(g0,g1)
    c: Coincident(g1,g2)
    c: Coincident(g2,g3)
    c: Coincident(g3,g0)
    c: Horizontal(g0)
    c: Horizontal(g2)
    c: Vertical(g1)
    c: Vertical(g3)
    c: Coincident(g0,g-4)
    c: Coincident(g1,g-6)
FEATURE [PartDesign::Body] Body002  label="Left-Fan-Clamp2-design"
  Group = -> [ShapeBinder001,Sketch036,Pad016,DatumPlane009,Sketch037,Pad017,DatumPlane010,Sketch038,Pad018,Sketch039,Pocket007008,DatumPlane011,Sketch040,Pocket007009,DatumPlane013,Sketch042,Pad019,DatumPlane014,Sketch043,Pocket007011,DatumPlane015,Sketch044]
  Origin = -> Origin002
  Placement = pos=(0,0,22) rot=(0,0,1;0rad)
  Tip = -> Pocket007011
FEATURE [PartDesign::ShapeBinder] ShapeBinder002
  Placement = pos=(-68,-32,-2.1e-15) rot=(1,0,0;1.5708rad)
  Support = -> [Sketch044]
  TraceSupport = false
FEATURE [Sketcher::SketchObject] Sketch045
  ExternalGeometry = -> [ShapeBinder002]
  MapMode = 5
  Placement = pos=(0,0,0) rot=(1,0,0;1.5708rad)
  Support = -> [XZ_Plane006]
  expr: Constraints[17] = FD_BaseDimension.Constraints.WallThickness_Small
  expr: Constraints[9] = FD_BaseDimension.Constraints.Clearance
  expr: Constraints[20] = FD_BaseDimension.Constraints.WallThickness_Small
  expr: Constraints[18] = FD_BaseDimension.Constraints.WallThickness_Small
  expr: Constraints[8] = FD_BaseDimension.Constraints.Clearance
  expr: Constraints[19] = FD_BaseDimension.Constraints.WallThickness_Small
  expr: Constraints[10] = FD_BaseDimension.Constraints.Clearance
  expr: Constraints[11] = FD_BaseDimension.Constraints.Clearance
  sketch-geometry (8):
    g0: LineSegment StartX=-65.15 StartY=17.4 StartZ=0 EndX=-54.6 EndY=17.4 EndZ=0
    g1: LineSegment StartX=-54.6 StartY=17.4 StartZ=0 EndX=-54.6 EndY=2.85 EndZ=0
    g2: LineSegment StartX=-54.6 StartY=2.85 StartZ=0 EndX=-65.15 EndY=2.85 EndZ=0
    g3: LineSegment StartX=-65.15 StartY=2.85 StartZ=0 EndX=-65.15 EndY=17.4 EndZ=0
    g4: LineSegment StartX=-55.6 StartY=16.4 StartZ=0 EndX=-55.6 EndY=3.85 EndZ=0
    g5: LineSegment StartX=-55.6 StartY=3.85 StartZ=0 EndX=-64.15 EndY=3.85 EndZ=0
    g6: LineSegment StartX=-64.15 StartY=3.85 StartZ=0 EndX=-64.15 EndY=16.4 EndZ=0
    g7: LineSegment StartX=-64.15 StartY=16.4 StartZ=0 EndX=-55.6 EndY=16.4 EndZ=0
  constraints (24):
    c: Coincident(g0,g1)
    c: Coincident(g1,g2)
    c: Coincident(g2,g3)
    c: Coincident(g3,g0)
    c: Horizontal(g0)
    c: Horizontal(g2)
    c: Vertical(g1)
    c: Vertical(g3)
    c: DistanceY(g0,g-4) = 0.6
    c: DistanceX(g-4,g0) = 0.6
    c: DistanceX(g0,g-5) = 0.6
    c: DistanceY(g-6,g2) = 0.6
    c: Coincident(g4,g5)
    c: Coincident(g5,g6)
    c: Horizontal(g5)
    c: Vertical(g4)
    c: Vertical(g6)
    c: DistanceX(g2,g5) = 1
    c: DistanceY(g2,g5) = 1
    c: DistanceX(g4,g1) = 1
    c: DistanceY(g6,g0) = 1
    c: Coincident(g7,g6)
    c: Coincident(g7,g4)
    c: Horizontal(g7)
FEATURE [PartDesign::Pad] Pad020  label="SnugglyFit_ToClamp"
  Length = 10
  Length2 = 100
  Placement = pos=(0,0,0) rot=(1,0,0;1.5708rad)
  Profile = -> Sketch045
  Reversed = true
  Type = 0
FEATURE [PartDesign::Pocket] Pocket007013  label="Lüfterbefestigungslöcher"
  BaseFeature = -> Pad025
  Length = 15
  Length2 = 100
  Placement = pos=(0,0,0) rot=(1,0,0;1.5708rad)
  Profile = -> Sketch052
  Reversed = true
  Type = 0
FEATURE [PartDesign::Mirrored] Mirrored  label="Mirror_Lüfertmountingtisch"
  BaseFeature = -> Pocket007013
  MirrorPlane = -> DatumPlane004
  Originals = -> [Pad025]
  Placement = pos=(0,0,0) rot=(1,0,0;1.5708rad)
FEATURE [PartDesign::Mirrored] Mirrored001  label="Mirror_Lüfterbefestigungslöcher"
  BaseFeature = -> Mirrored
  MirrorPlane = -> DatumPlane004
  Originals = -> [Pocket007013]
  Placement = pos=(0,0,0) rot=(1,0,0;1.5708rad)
FEATURE [PartDesign::Pocket] Pocket007014  label="TitanAbsenkung"
  BaseFeature = -> Mirrored001
  Length = 1.5
  Length2 = 100
  Placement = pos=(0,0,0) rot=(1,0,0;1.5708rad)
  Profile = -> Sketch023
  Type = 0
FEATURE [PartDesign::Body] Body  label="XY-Carrier-design"
  Group = -> [Sketch003,Sketch,DatumLine,Sketch001,DatumLine001,Sketch004,Pad,Sketch005,Pad001,DatumPlane,Sketch006,Pad002,Sketch007,Pad003,Sketch008,Pad004,DatumPlane001,Sketch009,Pocket,Sketch010,Pocket001,DatumPlane002,Sketch011,Pocket002,Sketch012,Sketch013,Sketch014,Pocket003,Sketch016,Pocket005,DatumPlane003,Sketch017,Pocket006,Pad014,Pad015,Pocket007003,DatumLine005,DatumLine006,DatumPlane004,Sketch018,+20 more]
  Origin = -> Origin
  Tip = -> Pocket007014
FEATURE [Sketcher::SketchObject] Sketch053  label="FD_BaseDimension"
  MapMode = 5
  Placement = pos=(0,0,0) rot=(1,0,0;1.5708rad)
  Support = -> [XZ_Plane006]
  sketch-geometry (3):
    g0: LineSegment [constr] StartX=-77.6491 StartY=47.6557 StartZ=0 EndX=-76.6491 EndY=47.6557 EndZ=0
    g1: LineSegment [constr] StartX=-78.0014 StartY=44.3485 StartZ=0 EndX=-77.4014 EndY=44.3485 EndZ=0
    g2: LineSegment [constr] StartX=-73.0784 StartY=47.1247 StartZ=0 EndX=-72.0784 EndY=47.1247 EndZ=0
  constraints (6):
    c: Horizontal(g0)
    c: DistanceX(g0,g0) = 1  'WallThickness_Regular'
    c: Horizontal(g1)
    c: DistanceX(g1,g1) = 0.6  'Clearance'
    c: Horizontal(g2)
    c: DistanceX(g2,g2) = 1  'WallThickness_Small'
FEATURE [PartDesign::Plane] DatumPlane022  label="PrintSurface"
  AttachmentOffset = pos=(0,0,0) rot=(0,1,0;1.5708rad)
  Length = 24
  MapMode = 7
  Placement = pos=(-65.15,-2.949e-13,2.85) rot=(0,1,0;4.71239rad)
  ResizeMode = 0
  Support = -> [Sketch045]
  Width = 24
FEATURE [Sketcher::SketchObject] Sketch046
  ExternalGeometry = -> [ShapeBinder002,Sketch045,DatumPlane022]
  MapMode = 5
  Placement = pos=(0,0,0) rot=(1,0,0;1.5708rad)
  Support = -> [XZ_Plane006]
  sketch-geometry (9):
    g0: LineSegment StartX=-65.15 StartY=18 StartZ=0 EndX=-52.4 EndY=18 EndZ=0
    g1: LineSegment StartX=-50.15 StartY=15.75 StartZ=0 EndX=-50.15 EndY=-5.75 EndZ=0
    g2: LineSegment StartX=-50.15 StartY=-5.75 StartZ=0 EndX=-65.15 EndY=-5.75 EndZ=0
    g3: LineSegment StartX=-65.15 StartY=-5.75 StartZ=0 EndX=-65.15 EndY=18 EndZ=0
    g4: LineSegment StartX=-64.15 StartY=3.85 StartZ=0 EndX=-55.6 EndY=3.85 EndZ=0
    g5: LineSegment StartX=-55.6 StartY=3.85 StartZ=0 EndX=-55.6 EndY=16.4 EndZ=0
    g6: LineSegment StartX=-55.6 StartY=16.4 StartZ=0 EndX=-64.15 EndY=16.4 EndZ=0
    g7: LineSegment StartX=-64.15 StartY=16.4 StartZ=0 EndX=-64.15 EndY=3.85 EndZ=0
    g8: LineSegment StartX=-52.4 StartY=18 StartZ=0 EndX=-50.15 EndY=15.75 EndZ=0
  constraints (25):
    c: Coincident(g1,g2)
    c: Coincident(g2,g3)
    c: Horizontal(g0)
    c: Horizontal(g2)
    c: Vertical(g1)
    c: Vertical(g3)
    c: Coincident(g4,g5)
    c: Coincident(g5,g6)
    c: Coincident(g6,g7)
    c: Coincident(g7,g4)
    c: Horizontal(g4)
    c: Horizontal(g6)
    c: Vertical(g5)
    c: Vertical(g7)
    c: Coincident(g0,g3)
    c: Coincident(g6,g-8)
    c: Coincident(g-7,g4)
    c: PointOnObject(g-5,g0)
    c: Coincident(g0,g8)
    c: Coincident(g8,g1)
    c: Angle(g8,g1) = 2.35619
    c: DistanceX(g0,g0) = 12.75
    c: DistanceY(g1,g1) = 21.5
    c: DistanceY(g3,g3) = 23.75
    c: PointOnObject(g0,g-10)
FEATURE [PartDesign::Pad] Pad021  label="FD_MakeItBigger"
  BaseFeature = -> Pad020
  Length = 1
  Length2 = 100
  Placement = pos=(0,0,0) rot=(1,0,0;1.5708rad)
  Profile = -> Sketch046
  Type = 0
FEATURE [PartDesign::Plane] DatumPlane016  label="FrontBiggerMakerPlate"
  AttachmentOffset = pos=(0,0,1) rot=(0,0,1;0rad)
  Length = 24
  MapMode = 2
  Placement = pos=(0,-1,-1.035e-13) rot=(1,0,0;1.5708rad)
  ResizeMode = 0
  Support = -> [Sketch046]
  Width = 24
  expr: AttachmentOffset.Base.z = Pad021.Length
FEATURE [Sketcher::SketchObject] Sketch047
  ExternalGeometry = -> [DatumPlane022,Sketch046]
  MapMode = 5
  Placement = pos=(0,-1,-1.035e-13) rot=(1,0,0;1.5708rad)
  Support = -> [DatumPlane016]
  expr: Constraints[29] = FD_BaseDimension.Constraints.WallThickness_Regular
  expr: Constraints[22] = FD_BaseDimension.Constraints.WallThickness_Regular
  expr: Constraints[21] = FD_BaseDimension.Constraints.WallThickness_Regular
  expr: Constraints[23] = FD_BaseDimension.Constraints.WallThickness_Regular
  expr: Constraints[19] = FD_BaseDimension.Constraints.WallThickness_Small
  sketch-geometry (11):
    g0: LineSegment StartX=-65.15 StartY=18 StartZ=0 EndX=-52.4 EndY=18 EndZ=0
    g1: LineSegment StartX=-50.15 StartY=15.75 StartZ=0 EndX=-50.15 EndY=-5.75 EndZ=0
    g2: LineSegment StartX=-50.15 StartY=-5.75 StartZ=0 EndX=-65.15 EndY=-5.75 EndZ=0
    g3: LineSegment StartX=-65.15 StartY=-5.75 StartZ=0 EndX=-65.15 EndY=18 EndZ=0
    g4: LineSegment StartX=-64.15 StartY=17 StartZ=0 EndX=-52.8142 EndY=17 EndZ=0
    g5: LineSegment StartX=-51.15 StartY=15.3358 StartZ=0 EndX=-51.15 EndY=-4.75 EndZ=0
    g6: LineSegment StartX=-51.15 StartY=-4.75 StartZ=0 EndX=-64.15 EndY=-4.75 EndZ=0
    g7: LineSegment StartX=-64.15 StartY=-4.75 StartZ=0 EndX=-64.15 EndY=17 EndZ=0
    g8: LineSegment StartX=-52.8142 StartY=17 StartZ=0 EndX=-51.15 EndY=15.3358 EndZ=0
    g9: LineSegment StartX=-52.4 StartY=18 StartZ=0 EndX=-50.15 EndY=15.75 EndZ=0
    g10: LineSegment [constr] StartX=-52.8142 StartY=17 StartZ=0 EndX=-52.1071 EndY=17.7071 EndZ=0
  constraints (31):
    c: Coincident(g1,g2)
    c: Coincident(g2,g3)
    c: Coincident(g3,g0)
    c: Horizontal(g0)
    c: Horizontal(g2)
    c: Vertical(g1)
    c: Vertical(g3)
    c: Coincident(g5,g6)
    c: Coincident(g6,g7)
    c: Coincident(g7,g4)
    c: Horizontal(g4)
    c: Horizontal(g6)
    c: Vertical(g5)
    c: Vertical(g7)
    c: PointOnObject(g0,g-3)
    c: Coincident(g8,g4)
    c: Coincident(g8,g5)
    c: Coincident(g9,g0)
    c: Parallel(g8,g9)
    c: DistanceX(g0,g4) = 1
    c: Coincident(g9,g1)
    c: DistanceY(g2,g6) = 1
    c: DistanceX(g5,g1) = 1
    c: DistanceY(g4,g0) = 1
    c: Coincident(g0,g-4)
    c: Coincident(g1,g-4)
    c: Coincident(g10,g4)
    c: PointOnObject(g10,g9)
    c: Perpendicular(g10,g9)
    c: Distance(g10) = 1
    c: PointOnObject(g-5,g2)
FEATURE [PartDesign::Pad] Pad022  label="FanDuct_Horizontal1"
  BaseFeature = -> Pad021
  Length = 18
  Length2 = 100
  Placement = pos=(0,0,0) rot=(1,0,0;1.5708rad)
  Profile = -> Sketch047
  Type = 0
FEATURE [PartDesign::Plane] DatumPlane017  label="FD_H1_FrontPlane"
  AttachmentOffset = pos=(0,0,18) rot=(0,0,1;0rad)
  Length = 24
  MapMode = 2
  Placement = pos=(0,-19,-1.966e-12) rot=(1,0,0;1.5708rad)
  ResizeMode = 0
  Support = -> [Sketch047]
  Width = 24
  expr: AttachmentOffset.Base.z = Pad022.Length
FEATURE [Sketcher::SketchObject] Sketch054
  ExternalGeometry = -> [DatumPlane022,Sketch046]
  MapMode = 5
  Placement = pos=(0,-19,-1.966e-12) rot=(1,0,0;1.5708rad)
  Support = -> [DatumPlane017]
  expr: Constraints[42] = FD_BaseDimension.Constraints.WallThickness_Regular
  expr: Constraints[43] = FD_BaseDimension.Constraints.WallThickness_Regular
  expr: Constraints[18] = FD_BaseDimension.Constraints.WallThickness_Regular
  expr: Constraints[17] = FD_BaseDimension.Constraints.WallThickness_Regular
  expr: Constraints[16] = FD_BaseDimension.Constraints.WallThickness_Regular
  expr: Constraints[15] = FD_BaseDimension.Constraints.WallThickness_Small
  sketch-geometry (15):
    g0: LineSegment StartX=-65.15 StartY=18 StartZ=0 EndX=-50.15 EndY=18 EndZ=0
    g1: LineSegment StartX=-50.15 StartY=-5.75 StartZ=0 EndX=-65.15 EndY=-5.75 EndZ=0
    g2: LineSegment StartX=-65.15 StartY=-5.75 StartZ=0 EndX=-65.15 EndY=18 EndZ=0
    g3: LineSegment StartX=-64.15 StartY=17 StartZ=0 EndX=-52.8142 EndY=17 EndZ=0
    g4: LineSegment StartX=-51.15 StartY=15.3358 StartZ=0 EndX=-51.15 EndY=-4.75 EndZ=0
    g5: LineSegment StartX=-51.15 StartY=-4.75 StartZ=0 EndX=-64.15 EndY=-4.75 EndZ=0
    g6: LineSegment StartX=-64.15 StartY=-4.75 StartZ=0 EndX=-64.15 EndY=17 EndZ=0
    g7: LineSegment StartX=-52.8142 StartY=17 StartZ=0 EndX=-51.15 EndY=15.3358 EndZ=0
    g8: LineSegment [constr] StartX=-52.8142 StartY=17 StartZ=0 EndX=-52.1071 EndY=17.7071 EndZ=0
    g9: LineSegment StartX=-50.15 StartY=-5.75 StartZ=0 EndX=-50.15 EndY=-2.6 EndZ=0
    g10: LineSegment StartX=-50.15 StartY=-2.6 StartZ=0 EndX=-41.15 EndY=-2.6 EndZ=0
    g11: LineSegment StartX=-41.15 StartY=-2.6 StartZ=0 EndX=-41.15 EndY=4.9 EndZ=0
    g12: LineSegment StartX=-41.15 StartY=4.9 StartZ=0 EndX=-50.15 EndY=4.9 EndZ=0
    g13: LineSegment StartX=-50.15 StartY=4.9 StartZ=0 EndX=-50.15 EndY=18 EndZ=0
    g14: Circle CenterX=-45.65 CenterY=1.05 CenterZ=0 NormalX=0 NormalY=0 NormalZ=1 AngleXU=0 Radius=2
  constraints (45):
    c: Coincident(g1,g2)
    c: Coincident(g2,g0)
    c: Horizontal(g0)
    c: Horizontal(g1)
    c: Vertical(g2)
    c: Coincident(g4,g5)
    c: Coincident(g5,g6)
    c: Coincident(g6,g3)
    c: Horizontal(g3)
    c: Horizontal(g5)
    c: Vertical(g4)
    c: Vertical(g6)
    c: PointOnObject(g0,g-3)
    c: Coincident(g7,g3)
    c: Coincident(g7,g4)
    c: DistanceX(g0,g3) = 1
    c: DistanceY(g1,g5) = 1
    c: DistanceX(g4,g1) = 1
    c: DistanceY(g3,g0) = 1
    c: Coincident(g8,g3)
    c: PointOnObject(g-5,g1)
    c: Coincident(g9,g1)
    c: Vertical(g9)
    c: Horizontal(g10)
    c: Coincident(g10,g11)
    c: Vertical(g11)
    c: Coincident(g11,g12)
    c: Horizontal(g12)
    c: Coincident(g12,g13)
    c: Vertical(g13)
    c: Equal(g10,g12)
    c: DistanceY(g11,g11) = 7.5
    c: Coincident(g10,g9)
    c: DistanceX(g9,g14) = 4.5
    c: DistanceY(g9,g14) = 3.65
    c: DistanceX(g12,g12) = 9
    c: Radius(g14) = 2
    c: DistanceY(g9,g9) = 3.15
    c: PointOnObject(g-4,g0)
    c: Coincident(g0,g13)
    c: PointOnObject(g8,g-4)
    c: Perpendicular(g8,g-4)
    c: DistanceX(g4,g-4) = 1
    c: Distance(g8) = 1
    c: Parallel(g7,g-4)
FEATURE [PartDesign::Pad] Pad026  label="FD_ScrewingTab"
  BaseFeature = -> Pad022
  Length = 2
  Length2 = 100
  Placement = pos=(0,0,0) rot=(1,0,0;1.5708rad)
  Profile = -> Sketch054
  Type = 0
FEATURE [PartDesign::Plane] DatumPlane023  label="FD_FrontOfScrewingTabPlane"
  AttachmentOffset = pos=(0,0,2) rot=(0,0,1;0rad)
  Length = 24
  MapMode = 2
  Placement = pos=(0,-21,-2.1729e-12) rot=(1,0,0;1.5708rad)
  ResizeMode = 0
  Support = -> [Sketch054]
  Width = 24
  expr: AttachmentOffset.Base.z = FD_ScrewingTab.Length
FEATURE [PartDesign::Plane] DatumPlane024  label="Opposite_From_PrintSurface"
  AttachmentOffset = pos=(0,0,0) rot=(0,1,0;1.5708rad)
  Length = 30.2887
  MapMode = 7
  Placement = pos=(-50.15,-1.6297e-12,15.75) rot=(0,1,0;4.71239rad)
  ResizeMode = 0
  Support = -> [Sketch046]
  Width = 24.5387
FEATURE [PartDesign::Plane] DatumPlane025  label="Bottom_Plane"
  AttachmentOffset = pos=(0,0,0) rot=(1,0,0;1.5708rad)
  Length = 26.9369
  MapMode = 7
  Placement = pos=(-50.15,5.95e-13,-5.75) rot=(0.707107,0.707107,0;3.14159rad)
  ResizeMode = 0
  Support = -> [Sketch046]
  Width = 67.0869
FEATURE [Sketcher::SketchObject] Sketch055
  ExternalGeometry = -> [DatumPlane023,Sketch054,DatumPlane025]
  MapMode = 5
  Placement = pos=(-65.15,-2.949e-13,2.85) rot=(0,-1,0;1.5708rad)
  Support = -> [DatumPlane022]
  expr: Constraints[25] = FD_BaseDimension.Constraints.WallThickness_Regular
  expr: Constraints[17] = FD_BaseDimension.Constraints.WallThickness_Regular
  sketch-geometry (10):
    g0: LineSegment StartX=-8.6 StartY=-21 StartZ=0 EndX=-8.6 EndY=-31.5 EndZ=0
    g1: LineSegment StartX=-8.6 StartY=-31.5 StartZ=0 EndX=5.15 EndY=-31.5 EndZ=0
    g2: LineSegment StartX=15.15 StartY=-21.5 StartZ=0 EndX=15.15 EndY=-21 EndZ=0
    g3: ArcOfCircle CenterX=5.15 CenterY=-21.5 CenterZ=0 NormalX=0 NormalY=0 NormalZ=1 AngleXU=0 Radius=10 StartAngle=4.71239 EndAngle=6.28319
    g4: LineSegment StartX=-7.6 StartY=-21 StartZ=0 EndX=-7.6 EndY=-30.5 EndZ=0
    g5: LineSegment StartX=-7.6 StartY=-30.5 StartZ=0 EndX=5.15 EndY=-30.5 EndZ=0
    g6: ArcOfCircle CenterX=5.15 CenterY=-21.5 CenterZ=0 NormalX=0 NormalY=0 NormalZ=1 AngleXU=0 Radius=9 StartAngle=4.71239 EndAngle=6.28318
    g7: LineSegment StartX=-7.6 StartY=-21 StartZ=0 EndX=-8.6 EndY=-21 EndZ=0
    g8: LineSegment StartX=14.15 StartY=-21 StartZ=0 EndX=15.15 EndY=-21 EndZ=0
    g9: LineSegment StartX=14.15 StartY=-21 StartZ=0 EndX=14.15 EndY=-21.5 EndZ=0
  constraints (29):
    c: Horizontal(g1)
    c: Vertical(g0)
    c: Vertical(g2)
    c: Tangent(g2,g3) = -1.5708
    c: Tangent(g1,g3) = -1.5708
    c: Horizontal(g5)
    c: Coincident(g6,g3)
    c: Coincident(g5,g4)
    c: Coincident(g7,g4)
    c: Coincident(g7,g0)
    c: Horizontal(g7)
    c: Coincident(g5,g6)
    c: Radius(g3) = 10
    c: Radius(g6) = 9
    c: Coincident(g8,g2)
    c: Horizontal(g8)
    c: PointOnObject(g-6,g2)
    c: DistanceX(g8,g8) = 1
    c: Coincident(g9,g8)
    c: Coincident(g9,g6)
    c: Vertical(g9)
    c: DistanceY(g2,g2) = 0.5
    c: PointOnObject(g2,g-3)
    c: Coincident(g0,g1)
    c: Vertical(g4)
    c: DistanceX(g7,g7) = 1
    c: PointOnObject(g0,g-3)
    c: PointOnObject(g0,g-7)
    c: DistanceY(g0,g4) = 1
FEATURE [PartDesign::Pad] Pad027  label="FD_Curve"
  BaseFeature = -> Pad026
  Length = 10
  Length2 = 100
  Placement = pos=(0,0,0) rot=(1,0,0;1.5708rad)
  Profile = -> Sketch055
  Reversed = true
  Type = 3
  UpToFace = -> DatumPlane024 [Plane]
FEATURE [Sketcher::SketchObject] Sketch057
  ExternalGeometry = -> [Pad027,Sketch055]
  MapMode = 5
  Placement = pos=(-50.15,-1.6297e-12,15.75) rot=(0,-1,0;1.5708rad)
  Support = -> [DatumPlane024]
  sketch-geometry (5):
    g0: LineSegment StartX=2.25 StartY=-21 StartZ=0 EndX=2.25 EndY=-21.5 EndZ=0
    g1: LineSegment StartX=-7.75 StartY=-31.5 StartZ=0 EndX=-21.5 EndY=-31.5 EndZ=0
    g2: LineSegment StartX=-21.5 StartY=-31.5 StartZ=0 EndX=-21.5 EndY=-21 EndZ=0
    g3: LineSegment StartX=-21.5 StartY=-21 StartZ=0 EndX=2.25 EndY=-21 EndZ=0
    g4: ArcOfCircle CenterX=-7.75 CenterY=-21.5 CenterZ=0 NormalX=0 NormalY=0 NormalZ=1 AngleXU=0 Radius=10 StartAngle=4.71239 EndAngle=6.28319
  constraints (11):
    c: Coincident(g0,g-6)
    c: Vertical(g0)
    c: Horizontal(g1)
    c: Coincident(g1,g2)
    c: Coincident(g2,g-4)
    c: Vertical(g2)
    c: Coincident(g2,g3)
    c: Coincident(g3,g0)
    c: Tangent(g0,g4) = 1.5708
    c: Tangent(g1,g4) = 1.5708
    c: Coincident(g4,g-5)
FEATURE [PartDesign::Pad] Pad028  label="FD_CurveLID"
  BaseFeature = -> Pad027
  Length = 1
  Length2 = 100
  Placement = pos=(0,0,0) rot=(1,0,0;1.5708rad)
  Profile = -> Sketch057
  Type = 0
  expr: Length = FD_BaseDimension.Constraints.WallThickness_Regular
FEATURE [Sketcher::SketchObject] Sketch058
  ExternalGeometry = -> [Sketch055]
  MapMode = 5
  Placement = pos=(-65.15,-2.949e-13,2.85) rot=(0,-1,0;1.5708rad)
  Support = -> [DatumPlane022]
  sketch-geometry (5):
    g0: LineSegment StartX=15.15 StartY=-21 StartZ=0 EndX=15.15 EndY=-21.5 EndZ=0
    g1: LineSegment StartX=5.15 StartY=-31.5 StartZ=0 EndX=-8.6 EndY=-31.5 EndZ=0
    g2: LineSegment StartX=-8.6 StartY=-31.5 StartZ=0 EndX=-8.6 EndY=-21 EndZ=0
    g3: LineSegment StartX=-8.6 StartY=-21 StartZ=0 EndX=15.15 EndY=-21 EndZ=0
    g4: ArcOfCircle CenterX=5.15 CenterY=-21.5 CenterZ=0 NormalX=0 NormalY=0 NormalZ=1 AngleXU=0 Radius=10 StartAngle=4.71239 EndAngle=6.28319
  constraints (11):
    c: Vertical(g0)
    c: Horizontal(g1)
    c: Coincident(g1,g2)
    c: Vertical(g2)
    c: Coincident(g2,g3)
    c: Coincident(g3,g0)
    c: Tangent(g0,g4) = 1.5708
    c: Tangent(g1,g4) = 1.5708
    c: Coincident(g4,g-4)
    c: Coincident(g2,g-3)
    c: Coincident(g-5,g0)
FEATURE [PartDesign::Pad] Pad029  label="CureveLID2"
  BaseFeature = -> Pad028
  Length = 1
  Length2 = 100
  Placement = pos=(0,0,0) rot=(1,0,0;1.5708rad)
  Profile = -> Sketch058
  Reversed = true
  Type = 0
  expr: Length = FD_BaseDimension.Constraints.WallThickness_Small
FEATURE [Sketcher::SketchObject] Sketch059
  ExternalGeometry = -> [Pad029,Sketch057]
  MapMode = 5
  Placement = pos=(-50.15,5.95e-13,-5.75) rot=(0.707107,0.707107,0;3.14159rad)
  Support = -> [DatumPlane025]
  expr: Constraints[10] = 1.5 * FD_BaseDimension.Constraints.WallThickness_Regular
  expr: Constraints[9] = FD_BaseDimension.Constraints.WallThickness_Small
  expr: Constraints[8] = FD_BaseDimension.Constraints.WallThickness_Regular
  sketch-geometry (4):
    g0: LineSegment StartX=-3 StartY=-1 StartZ=0 EndX=-30 EndY=-1 EndZ=0
    g1: LineSegment StartX=-30 StartY=-1 StartZ=0 EndX=-30 EndY=-14 EndZ=0
    g2: LineSegment StartX=-30 StartY=-14 StartZ=0 EndX=-3 EndY=-14 EndZ=0
    g3: LineSegment StartX=-3 StartY=-14 StartZ=0 EndX=-3 EndY=-1 EndZ=0
  constraints (12):
    c: Coincident(g0,g1)
    c: Coincident(g1,g2)
    c: Coincident(g2,g3)
    c: Coincident(g3,g0)
    c: Horizontal(g0)
    c: Horizontal(g2)
    c: Vertical(g1)
    c: Vertical(g3)
    c: DistanceY(g0,g-4) = 1
    c: DistanceY(g-3,g2) = 1
    c: DistanceX(g-3,g1) = 1.5
    c: DistanceX(g2,g2) = 27
FEATURE [PartDesign::Pocket] Pocket007015
  BaseFeature = -> Pad029
  Length = 5
  Length2 = 100
  Placement = pos=(0,0,0) rot=(1,0,0;1.5708rad)
  Profile = -> Sketch059
  Type = 0
FEATURE [Sketcher::SketchObject] Sketch060  label="InterfaceToDüse"
  ExternalGeometry = -> [Sketch059]
  MapMode = 5
  Placement = pos=(-50.15,5.95e-13,-5.75) rot=(0.707107,0.707107,0;3.14159rad)
  Support = -> [DatumPlane025]
  expr: Constraints[20] = FD_BaseDimension.Constraints.WallThickness_Small
  expr: Constraints[19] = 2 * FD_BaseDimension.Constraints.WallThickness_Regular
  expr: Constraints[18] = FD_BaseDimension.Constraints.WallThickness_Regular
  expr: Constraints[16] = 1.5 * FD_BaseDimension.Constraints.WallThickness_Regular
  sketch-geometry (8):
    g0: LineSegment StartX=-31.5 StartY=0 StartZ=0 EndX=-1 EndY=0 EndZ=0
    g1: LineSegment StartX=-1 StartY=0 StartZ=0 EndX=-1 EndY=-15 EndZ=0
    g2: LineSegment StartX=-1 StartY=-15 StartZ=0 EndX=-31.5 EndY=-15 EndZ=0
    g3: LineSegment StartX=-31.5 StartY=-15 StartZ=0 EndX=-31.5 EndY=0 EndZ=0
    g4: LineSegment StartX=-30 StartY=-1 StartZ=0 EndX=-3 EndY=-1 EndZ=0
    g5: LineSegment StartX=-3 StartY=-1 StartZ=0 EndX=-3 EndY=-14 EndZ=0
    g6: LineSegment StartX=-3 StartY=-14 StartZ=0 EndX=-30 EndY=-14 EndZ=0
    g7: LineSegment StartX=-30 StartY=-14 StartZ=0 EndX=-30 EndY=-1 EndZ=0
  constraints (22):
    c: Coincident(g0,g1)
    c: Coincident(g1,g2)
    c: Coincident(g2,g3)
    c: Coincident(g3,g0)
    c: Horizontal(g0)
    c: Horizontal(g2)
    c: Vertical(g1)
    c: Vertical(g3)
    c: Coincident(g4,g5)
    c: Coincident(g5,g6)
    c: Coincident(g6,g7)
    c: Coincident(g7,g4)
    c: Horizontal(g4)
    c: Horizontal(g6)
    c: Vertical(g5)
    c: Vertical(g7)
    c: DistanceX(g2,g6) = 1.5
    c: Coincident(g6,g-5)
    c: DistanceY(g4,g0) = 1
    c: DistanceX(g4,g0) = 2
    c: DistanceY(g1,g5) = 1
    c: Coincident(g-6,g4)
FEATURE [PartDesign::Pad] Pad030  label="Fanduct_Part1"
  BaseFeature = -> Pocket007015
  Length = 30
  Length2 = 100
  Placement = pos=(0,0,0) rot=(1,0,0;1.5708rad)
  Profile = -> Sketch060
  Type = 0
FEATURE [PartDesign::ShapeBinder] ShapeBinder003
  Placement = pos=(-50.15,5.95e-13,-5.75) rot=(0.707107,0.707107,0;3.14159rad)
  Support = -> [Sketch060]
  TraceSupport = false
FEATURE [Sketcher::SketchObject] Sketch061
  ExternalGeometry = -> [ShapeBinder003]
  MapMode = 5
  expr: Constraints[23] = FD_BaseDimension.Constraints.WallThickness_Small
  expr: Constraints[21] = FD_BaseDimension.Constraints.WallThickness_Small
  expr: Constraints[20] = FD_BaseDimension.Constraints.WallThickness_Small
  expr: Constraints[11] = FD_BaseDimension.Constraints.Clearance
  expr: Constraints[10] = FD_BaseDimension.Constraints.Clearance
  expr: Constraints[22] = FD_BaseDimension.Constraints.WallThickness_Small
  expr: Constraints[9] = FD_BaseDimension.Constraints.Clearance
  expr: Constraints[8] = FD_BaseDimension.Constraints.Clearance
  sketch-geometry (8):
    g0: LineSegment StartX=-63.55 StartY=-3.6 StartZ=0 EndX=-51.75 EndY=-3.6 EndZ=0
    g1: LineSegment StartX=-51.75 StartY=-3.6 StartZ=0 EndX=-51.75 EndY=-29.4 EndZ=0
    g2: LineSegment StartX=-51.75 StartY=-29.4 StartZ=0 EndX=-63.55 EndY=-29.4 EndZ=0
    g3: LineSegment StartX=-63.55 StartY=-29.4 StartZ=0 EndX=-63.55 EndY=-3.6 EndZ=0
    g4: LineSegment StartX=-62.55 StartY=-4.6 StartZ=0 EndX=-52.75 EndY=-4.6 EndZ=0
    g5: LineSegment StartX=-52.75 StartY=-4.6 StartZ=0 EndX=-52.75 EndY=-28.4 EndZ=0
    g6: LineSegment StartX=-52.75 StartY=-28.4 StartZ=0 EndX=-62.55 EndY=-28.4 EndZ=0
    g7: LineSegment StartX=-62.55 StartY=-28.4 StartZ=0 EndX=-62.55 EndY=-4.6 EndZ=0
  constraints (24):
    c: Coincident(g0,g1)
    c: Coincident(g1,g2)
    c: Coincident(g2,g3)
    c: Coincident(g3,g0)
    c: Horizontal(g0)
    c: Horizontal(g2)
    c: Vertical(g1)
    c: Vertical(g3)
    c: DistanceX(g-6,g2) = 0.6
    c: DistanceY(g-6,g2) = 0.6
    c: DistanceY(g0,g-5) = 0.6
    c: DistanceX(g0,g-5) = 0.6
    c: Coincident(g4,g5)
    c: Coincident(g5,g6)
    c: Coincident(g6,g7)
    c: Coincident(g7,g4)
    c: Horizontal(g4)
    c: Horizontal(g6)
    c: Vertical(g5)
    c: Vertical(g7)
    c: DistanceX(g0,g4) = 1
    c: DistanceY(g4,g0) = 1
    c: DistanceY(g1,g5) = 1
    c: DistanceX(g5,g1) = 1
FEATURE [PartDesign::Pad] Pad031
  Length = 15
  Length2 = 100
  Profile = -> Sketch061
  Type = 0
FEATURE [Sketcher::SketchObject] Sketch062
  ExternalGeometry = -> [Sketch061,ShapeBinder003]
  MapMode = 5
  sketch-geometry (8):
    g0: LineSegment StartX=-52.75 StartY=-4.6 StartZ=0 EndX=-62.55 EndY=-4.6 EndZ=0
    g1: LineSegment StartX=-62.55 StartY=-4.6 StartZ=0 EndX=-62.55 EndY=-28.4 EndZ=0
    g2: LineSegment StartX=-62.55 StartY=-28.4 StartZ=0 EndX=-52.75 EndY=-28.4 EndZ=0
    g3: LineSegment StartX=-52.75 StartY=-28.4 StartZ=0 EndX=-52.75 EndY=-4.6 EndZ=0
    g4: LineSegment StartX=-65.15 StartY=-31.5 StartZ=0 EndX=-50.15 EndY=-31.5 EndZ=0
    g5: LineSegment StartX=-50.15 StartY=-31.5 StartZ=0 EndX=-50.15 EndY=-1 EndZ=0
    g6: LineSegment StartX=-50.15 StartY=-1 StartZ=0 EndX=-65.15 EndY=-1 EndZ=0
    g7: LineSegment StartX=-65.15 StartY=-1 StartZ=0 EndX=-65.15 EndY=-31.5 EndZ=0
  constraints (20):
    c: Coincident(g0,g1)
    c: Coincident(g1,g2)
    c: Coincident(g2,g3)
    c: Coincident(g3,g0)
    c: Horizontal(g0)
    c: Horizontal(g2)
    c: Vertical(g1)
    c: Vertical(g3)
    c: Coincident(g0,g-3)
    c: Coincident(g1,g-4)
    c: Coincident(g4,g5)
    c: Coincident(g5,g6)
    c: Coincident(g6,g7)
    c: Coincident(g7,g4)
    c: Horizontal(g4)
    c: Horizontal(g6)
    c: Vertical(g5)
    c: Vertical(g7)
    c: Coincident(g6,g-5)
    c: Coincident(g-6,g4)
FEATURE [PartDesign::Pad] Pad032
  BaseFeature = -> Pad031
  Length = 1
  Length2 = 100
  Profile = -> Sketch062
  Reversed = true
  Type = 0
FEATURE [PartDesign::Plane] DatumPlane026  label="Pad032_Plane"
  AttachmentOffset = pos=(0,0,-1) rot=(0,0,1;0rad)
  Length = 24
  MapMode = 2
  Placement = pos=(0,0,1) rot=(0,1,0;3.14159rad)
  ResizeMode = 0
  Support = -> [Sketch062]
  Width = 24
  expr: AttachmentOffset.Base.z = -Pad032.Length
FEATURE [Sketcher::SketchObject] Sketch063
  ExternalGeometry = -> [Sketch062]
  MapMode = 5
  Placement = pos=(0,0,1) rot=(0,1,0;3.14159rad)
  Support = -> [DatumPlane026]
  expr: Constraints[21] = FD_BaseDimension.Constraints.WallThickness_Regular
  expr: Constraints[20] = FD_BaseDimension.Constraints.WallThickness_Regular
  expr: Constraints[19] = FD_BaseDimension.Constraints.WallThickness_Regular
  expr: Constraints[18] = FD_BaseDimension.Constraints.WallThickness_Regular
  sketch-geometry (8):
    g0: LineSegment StartX=50.15 StartY=-1 StartZ=0 EndX=65.15 EndY=-1 EndZ=0
    g1: LineSegment StartX=65.15 StartY=-1 StartZ=0 EndX=65.15 EndY=-31.5 EndZ=0
    g2: LineSegment StartX=65.15 StartY=-31.5 StartZ=0 EndX=50.15 EndY=-31.5 EndZ=0
    g3: LineSegment StartX=50.15 StartY=-31.5 StartZ=0 EndX=50.15 EndY=-1 EndZ=0
    g4: LineSegment StartX=51.15 StartY=-2 StartZ=0 EndX=64.15 EndY=-2 EndZ=0
    g5: LineSegment StartX=64.15 StartY=-2 StartZ=0 EndX=64.15 EndY=-30.5 EndZ=0
    g6: LineSegment StartX=64.15 StartY=-30.5 StartZ=0 EndX=51.15 EndY=-30.5 EndZ=0
    g7: LineSegment StartX=51.15 StartY=-30.5 StartZ=0 EndX=51.15 EndY=-2 EndZ=0
  constraints (22):
    c: Coincident(g0,g1)
    c: Coincident(g1,g2)
    c: Coincident(g2,g3)
    c: Coincident(g3,g0)
    c: Horizontal(g0)
    c: Horizontal(g2)
    c: Vertical(g1)
    c: Vertical(g3)
    c: Coincident(g0,g-3)
    c: Coincident(g1,g-4)
    c: Coincident(g4,g5)
    c: Coincident(g5,g6)
    c: Coincident(g6,g7)
    c: Coincident(g7,g4)
    c: Horizontal(g4)
    c: Horizontal(g6)
    c: Vertical(g5)
    c: Vertical(g7)
    c: DistanceX(g4,g0) = 1
    c: DistanceX(g0,g4) = 1
    c: DistanceY(g2,g6) = 1
    c: DistanceY(g4,g0) = 1
FEATURE [PartDesign::Pad] Pad033
  BaseFeature = -> Pad032
  Length = 15
  Length2 = 100
  Profile = -> Sketch063
  Type = 0
FEATURE [PartDesign::Plane] DatumPlane027
  AttachmentOffset = pos=(0,0,0) rot=(0,1,0;1.5708rad)
  Length = 82.9037
  MapMode = 7
  Placement = pos=(-65.15,-31.5,1) rot=(1,0,0;1.5708rad)
  ResizeMode = 0
  Support = -> [Sketch063]
  Width = 27.7537
FEATURE [PartDesign::Plane] DatumPlane028
  AttachmentOffset = pos=(0,0,15) rot=(0,0,1;0rad)
  Length = 24
  MapMode = 2
  Placement = pos=(0,0,-14) rot=(0,1,0;3.14159rad)
  ResizeMode = 0
  Support = -> [Sketch063]
  Width = 24
  expr: AttachmentOffset.Base.z = Pad033.Length
FEATURE [Sketcher::SketchObject] Sketch064
  ExternalGeometry = -> [Sketch063,DatumPlane028]
  MapMode = 5
  Placement = pos=(-65.15,-31.5,1) rot=(1,0,0;1.5708rad)
  Support = -> [DatumPlane027]
  sketch-geometry (5):
    g0: LineSegment [constr] StartX=15 StartY=-3.2e-15 StartZ=0 EndX=15 EndY=-15 EndZ=0
    g1: LineSegment [constr] StartX=0 StartY=0 StartZ=0 EndX=0 EndY=-15 EndZ=0
    g2: LineSegment StartX=15 StartY=-15 StartZ=0 EndX=0 EndY=-10.9808 EndZ=0
    g3: LineSegment StartX=0 StartY=-10.9808 StartZ=0 EndX=0 EndY=-15 EndZ=0
    g4: LineSegment StartX=0 StartY=-15 StartZ=0 EndX=15 EndY=-15 EndZ=0
  constraints (13):
    c: Coincident(g0,g-4)
    c: PointOnObject(g0,g-5)
    c: Vertical(g0)
    c: Coincident(g1,g-1)
    c: PointOnObject(g1,g-5)
    c: Vertical(g1)
    c: Coincident(g2,g0)
    c: PointOnObject(g2,g1)
    c: Coincident(g3,g2)
    c: Coincident(g3,g1)
    c: Coincident(g4,g3)
    c: Coincident(g4,g2)
    c: Angle(g2,g4) = 0.261799
FEATURE [PartDesign::Pocket] Pocket007016
  BaseFeature = -> Pad033
  Length = 5
  Length2 = 100
  Profile = -> Sketch064
  Type = 1
FEATURE [Sketcher::SketchObject] Sketch065
  ExternalGeometry = -> [Sketch064,Pocket007016]
  MapMode = 5
  Placement = pos=(-6.85941,6.8e-15,-25.5997) rot=(0.991445,0,-0.130526;3.14159rad)
  Support = -> [Pocket007016]
  sketch-geometry (4):
    g0: LineSegment StartX=-60.3469 StartY=1 StartZ=0 EndX=-45.3177 EndY=1 EndZ=0
    g1: LineSegment StartX=-45.3177 StartY=1 StartZ=0 EndX=-45.3177 EndY=30.5 EndZ=0
    g2: LineSegment StartX=-45.3177 StartY=30.5 StartZ=0 EndX=-60.3469 EndY=30.5 EndZ=0
    g3: LineSegment StartX=-60.3469 StartY=30.5 StartZ=0 EndX=-60.3469 EndY=1 EndZ=0
  constraints (10):
    c: Coincident(g0,g1)
    c: Coincident(g1,g2)
    c: Coincident(g2,g3)
    c: Coincident(g3,g0)
    c: Horizontal(g2)
    c: Vertical(g1)
    c: Vertical(g3)
    c: Coincident(g0,g-4)
    c: PointOnObject(g0,g-4)
    c: DistanceX(g0,g-4) = 0.5
FEATURE [PartDesign::Fillet] Fillet
  Base = -> Pad030 [Edge50,Edge138]
  BaseFeature = -> Pad030
  Placement = pos=(0,0,0) rot=(1,0,0;1.5708rad)
  Radius = 2
FEATURE [PartDesign::Body] Body003  label="Left-Fan-Fanduct-design"
  Group = -> [ShapeBinder002,Sketch053,DatumPlane022,DatumPlane024,DatumPlane025,Sketch045,Pad020,Sketch046,Pad021,DatumPlane016,Sketch047,Pad022,DatumPlane017,Sketch054,Pad026,DatumPlane023,Sketch055,Pad027,Sketch057,Pad028,Sketch058,Pad029,Sketch059,Pocket007015,Sketch060,Pad030,Fillet]
  Origin = -> Origin006
  Placement = pos=(0,-32,22) rot=(0,0,1;0rad)
  Tip = -> Fillet
FEATURE [PartDesign::ShapeBinder] ShapeBinder004
  Support = -> [Sketch060]
  TraceSupport = false
FEATURE [Sketcher::SketchObject] Sketch067
  ExternalGeometry = -> [ShapeBinder004]
  MapMode = 5
  Support = -> [XY_Plane007]
  expr: Constraints[23] = FD_BaseDimension.Constraints.WallThickness_Small
  expr: Constraints[21] = FD_BaseDimension.Constraints.WallThickness_Small
  expr: Constraints[18] = FD_BaseDimension.Constraints.Clearance
  expr: Constraints[22] = FD_BaseDimension.Constraints.WallThickness_Small
  expr: Constraints[17] = FD_BaseDimension.Constraints.Clearance
  expr: Constraints[16] = FD_BaseDimension.Constraints.Clearance
  expr: Constraints[20] = FD_BaseDimension.Constraints.WallThickness_Small
  expr: Constraints[15] = FD_BaseDimension.Constraints.Clearance
  sketch-geometry (8):
    g0: LineSegment StartX=-63.55 StartY=-3.6 StartZ=0 EndX=-51.75 EndY=-3.6 EndZ=0
    g1: LineSegment StartX=-51.75 StartY=-3.6 StartZ=0 EndX=-51.75 EndY=-29.4 EndZ=0
    g2: LineSegment StartX=-51.75 StartY=-29.4 StartZ=0 EndX=-63.55 EndY=-29.4 EndZ=0
    g3: LineSegment StartX=-63.55 StartY=-29.4 StartZ=0 EndX=-63.55 EndY=-3.6 EndZ=0
    g4: LineSegment StartX=-62.55 StartY=-4.6 StartZ=0 EndX=-52.75 EndY=-4.6 EndZ=0
    g5: LineSegment StartX=-52.75 StartY=-4.6 StartZ=0 EndX=-52.75 EndY=-28.4 EndZ=0
    g6: LineSegment StartX=-52.75 StartY=-28.4 StartZ=0 EndX=-62.55 EndY=-28.4 EndZ=0
    g7: LineSegment StartX=-62.55 StartY=-28.4 StartZ=0 EndX=-62.55 EndY=-4.6 EndZ=0
  constraints (24):
    c: Coincident(g0,g1)
    c: Coincident(g1,g2)
    c: Coincident(g3,g0)
    c: Horizontal(g0)
    c: Horizontal(g2)
    c: Vertical(g1)
    c: Vertical(g3)
    c: Coincident(g4,g5)
    c: Coincident(g5,g6)
    c: Coincident(g6,g7)
    c: Coincident(g7,g4)
    c: Horizontal(g4)
    c: Horizontal(g6)
    c: Vertical(g5)
    c: Vertical(g7)
    c: DistanceX(g0,g-6) = 0.6
    c: DistanceY(g0,g-6) = 0.6
    c: DistanceX(g-5,g0) = 0.6
    c: DistanceY(g-5,g2) = 0.6
    c: Coincident(g3,g2)
    c: DistanceX(g0,g4) = 1
    c: DistanceY(g4,g0) = 1
    c: DistanceX(g4,g0) = 1
    c: DistanceY(g2,g6) = 1
FEATURE [PartDesign::Pad] Pad035
  Length = 15
  Length2 = 100
  Profile = -> Sketch067
  Type = 0
  expr: Length = Pad031.Length
FEATURE [PartDesign::ShapeBinder] ShapeBinder005
  Support = -> [Sketch062]
  TraceSupport = false
FEATURE [Sketcher::SketchObject] Sketch068
  AttachmentOffset = pos=(0,0,1) rot=(0,0,1;0rad)
  ExternalGeometry = -> [ShapeBinder005]
  MapMode = 5
  Placement = pos=(0,0,1) rot=(0,0,1;0rad)
  Support = -> [XY_Plane007]
  sketch-geometry (8):
    g0: LineSegment StartX=-62.55 StartY=-4.6 StartZ=0 EndX=-52.75 EndY=-4.6 EndZ=0
    g1: LineSegment StartX=-52.75 StartY=-4.6 StartZ=0 EndX=-52.75 EndY=-28.4 EndZ=0
    g2: LineSegment StartX=-52.75 StartY=-28.4 StartZ=0 EndX=-62.55 EndY=-28.4 EndZ=0
    g3: LineSegment StartX=-62.55 StartY=-28.4 StartZ=0 EndX=-62.55 EndY=-4.6 EndZ=0
    g4: LineSegment StartX=-65.15 StartY=-31.5 StartZ=0 EndX=-50.15 EndY=-31.5 EndZ=0
    g5: LineSegment StartX=-50.15 StartY=-31.5 StartZ=0 EndX=-50.15 EndY=-1 EndZ=0
    g6: LineSegment StartX=-50.15 StartY=-1 StartZ=0 EndX=-65.15 EndY=-1 EndZ=0
    g7: LineSegment StartX=-65.15 StartY=-1 StartZ=0 EndX=-65.15 EndY=-31.5 EndZ=0
  constraints (20):
    c: Coincident(g0,g1)
    c: Coincident(g1,g2)
    c: Coincident(g2,g3)
    c: Coincident(g3,g0)
    c: Horizontal(g0)
    c: Horizontal(g2)
    c: Vertical(g1)
    c: Vertical(g3)
    c: Coincident(g0,g-5)
    c: Coincident(g1,g-6)
    c: Coincident(g4,g5)
    c: Coincident(g5,g6)
    c: Coincident(g6,g7)
    c: Coincident(g7,g4)
    c: Horizontal(g4)
    c: Horizontal(g6)
    c: Vertical(g5)
    c: Vertical(g7)
    c: Coincident(g4,g-4)
    c: Coincident(g5,g-3)
FEATURE [PartDesign::Pad] Pad036
  BaseFeature = -> Pad035
  Length = 2
  Length2 = 100
  Profile = -> Sketch068
  Reversed = true
  Type = 0
  expr: Length = 2mm
FEATURE [PartDesign::ShapeBinder] ShapeBinder006
  Support = -> [Sketch063]
  TraceSupport = false
FEATURE [PartDesign::Plane] DatumPlane029
  AttachmentOffset = pos=(0,0,-2) rot=(0,0,1;0rad)
  Length = 74.1863
  MapMode = 13
  Placement = pos=(-55.15,-21.3333,-1) rot=(0,0,1;0rad)
  ResizeMode = 0
  Support = -> [Sketch068]
  Width = 40.3696
  expr: AttachmentOffset.Base.z = -Pad036.Length
FEATURE [Sketcher::SketchObject] Sketch069
  ExternalGeometry = -> [ShapeBinder006]
  MapMode = 5
  Placement = pos=(-55.15,-21.3333,-1) rot=(0,0,1;0rad)
  Support = -> [DatumPlane029]
  sketch-geometry (8):
    g0: LineSegment StartX=-10 StartY=20.3333 StartZ=0 EndX=5 EndY=20.3333 EndZ=0
    g1: LineSegment StartX=5 StartY=20.3333 StartZ=0 EndX=5 EndY=-10.1667 EndZ=0
    g2: LineSegment StartX=5 StartY=-10.1667 StartZ=0 EndX=-10 EndY=-10.1667 EndZ=0
    g3: LineSegment StartX=-10 StartY=-10.1667 StartZ=0 EndX=-10 EndY=20.3333 EndZ=0
    g4: LineSegment StartX=4 StartY=19.3333 StartZ=0 EndX=-9 EndY=19.3333 EndZ=0
    g5: LineSegment StartX=-9 StartY=19.3333 StartZ=0 EndX=-9 EndY=-9.16667 EndZ=0
    g6: LineSegment StartX=-9 StartY=-9.16667 StartZ=0 EndX=4 EndY=-9.16667 EndZ=0
    g7: LineSegment StartX=4 StartY=-9.16667 StartZ=0 EndX=4 EndY=19.3333 EndZ=0
  constraints (20):
    c: Coincident(g0,g1)
    c: Coincident(g1,g2)
    c: Coincident(g2,g3)
    c: Coincident(g3,g0)
    c: Horizontal(g0)
    c: Horizontal(g2)
    c: Vertical(g1)
    c: Vertical(g3)
    c: Coincident(g0,g-3)
    c: Coincident(g1,g-4)
    c: Coincident(g4,g5)
    c: Coincident(g5,g6)
    c: Coincident(g6,g7)
    c: Coincident(g7,g4)
    c: Horizontal(g4)
    c: Horizontal(g6)
    c: Vertical(g5)
    c: Vertical(g7)
    c: Coincident(g4,g-6)
    c: Coincident(g5,g-5)
FEATURE [Sketcher::SketchObject] Sketch077
  MapMode = 5
  Support = -> [XY_Plane007]
  sketch-geometry (4):
    g0: LineSegment StartX=-25.23 StartY=42.315 StartZ=0 EndX=0 EndY=42.315 EndZ=0
    g1: LineSegment StartX=0 StartY=42.315 StartZ=0 EndX=0 EndY=-42.315 EndZ=0
    g2: LineSegment StartX=0 StartY=-42.315 StartZ=0 EndX=-25.23 EndY=-42.315 EndZ=0
    g3: LineSegment StartX=-25.23 StartY=-42.315 StartZ=0 EndX=-25.23 EndY=42.315 EndZ=0
  constraints (11):
    c: Coincident(g0,g1)
    c: Coincident(g1,g2)
    c: Coincident(g2,g3)
    c: Coincident(g3,g0)
    c: Horizontal(g0)
    c: Horizontal(g2)
    c: Vertical(g3)
    c: PointOnObject(g0,g-2)
    c: Symmetric(g0,g1,g-1)
    c: DistanceX(g2,g2) = 25.23
    c: DistanceY(g1,g1) = 84.63
FEATURE [Sketcher::SketchObject] Sketch078
  MapMode = 5
  Placement = pos=(0,0,0) rot=(0.57735,0.57735,0.57735;2.0944rad)
  Support = -> [YZ_Plane007]
FEATURE [PartDesign::Plane] DatumPlane032
  AttachmentOffset = pos=(0,0,0) rot=(0,1,0;1.5708rad)
  Length = 58.7843
  MapMode = 7
  Placement = pos=(-25.23,-42.315,0) rot=(0.57735,0.57735,0.57735;2.0944rad)
  ResizeMode = 0
  Support = -> [Sketch077]
  Width = 26.4693
FEATURE [PartDesign::Plane] DatumPlane033
  Length = 24
  MapMode = 2
  ResizeMode = 0
  Support = -> [Sketch067]
  Width = 24
FEATURE [Sketcher::SketchObject] Sketch080
  ExternalGeometry = -> [Sketch067]
  MapMode = 5
  Support = -> [DatumPlane033]
  sketch-geometry (6):
    g0: Circle CenterX=-63.55 CenterY=-11.1 CenterZ=0 NormalX=0 NormalY=0 NormalZ=1 AngleXU=0 Radius=0.67
    g1: Circle CenterX=-63.55 CenterY=-21.9 CenterZ=0 NormalX=0 NormalY=0 NormalZ=1 AngleXU=0 Radius=0.67
    g2: Circle CenterX=-51.75 CenterY=-21.9 CenterZ=0 NormalX=0 NormalY=0 NormalZ=1 AngleXU=0 Radius=0.67
    g3: Circle CenterX=-51.75 CenterY=-11.1 CenterZ=0 NormalX=0 NormalY=0 NormalZ=1 AngleXU=0 Radius=0.67
    g4: Circle CenterX=-57.65 CenterY=-3.6 CenterZ=0 NormalX=0 NormalY=0 NormalZ=1 AngleXU=0 Radius=0.67
    g5: Circle CenterX=-57.65 CenterY=-29.4 CenterZ=0 NormalX=0 NormalY=0 NormalZ=1 AngleXU=0 Radius=0.67
  constraints (17):
    c: PointOnObject(g0,g-3)
    c: PointOnObject(g1,g-3)
    c: PointOnObject(g2,g-4)
    c: PointOnObject(g3,g-4)
    c: Horizontal(g3,g0)
    c: Horizontal(g2,g1)
    c: PointOnObject(g4,g-5)
    c: Vertical(g5,g4)
    c: Radius(g4) = 0.67
    c: Equal(g4,g0)
    c: Equal(g4,g1)
    c: Equal(g4,g5)
    c: Equal(g4,g2)
    c: Equal(g4,g3)
    c: Symmetric(g-6,g-6,g5)
    c: DistanceY(g0,g-5) = 7.5
    c: DistanceY(g-6,g1) = 7.5
FEATURE [PartDesign::Pad] Pad041
  BaseFeature = -> Pad036
  Length = 7.5
  Length2 = 100
  Profile = -> Sketch080
  Type = 0
FEATURE [PartDesign::Pad] Pad037
  BaseFeature = -> Pad041
  Length = 13
  Length2 = 100
  Profile = -> Sketch069
  Reversed = true
  Type = 0
  expr: Length = Pad033.Length - 2mm
FEATURE [PartDesign::Plane] DatumPlane030
  Length = 24
  MapMode = 5
  Placement = pos=(0,0,-14) rot=(1,0,0;3.14159rad)
  ResizeMode = 0
  Support = -> [Pad037]
  Width = 24
FEATURE [Sketcher::SketchObject] Sketch071
  ExternalGeometry = -> [Sketch069]
  MapMode = 5
  Placement = pos=(0,0,-14) rot=(1,0,0;3.14159rad)
  Support = -> [DatumPlane030]
  sketch-geometry (10):
    g0: LineSegment StartX=-65.15 StartY=31.5 StartZ=0 EndX=-50.0657 EndY=31.5 EndZ=0
    g1: LineSegment StartX=-62.6516 StartY=1 StartZ=0 EndX=-65.15 EndY=1 EndZ=0
    g2: LineSegment StartX=-65.15 StartY=1 StartZ=0 EndX=-65.15 EndY=31.5 EndZ=0
    g3: ArcOfCircle CenterX=-35.1544 CenterY=7.5 CenterZ=0 NormalX=0 NormalY=0 NormalZ=1 AngleXU=0 Radius=28.255 StartAngle=3.37372 EndAngle=8.40992
    g4: ArcOfCircle CenterX=-35.1544 CenterY=7.5 CenterZ=0 NormalX=0 NormalY=0 NormalZ=1 AngleXU=0 Radius=20.37 StartAngle=3.88501 EndAngle=8.68136
    g5: LineSegment StartX=-51.15 StartY=2 StartZ=0 EndX=-64.15 EndY=2 EndZ=0
    g6: LineSegment StartX=-64.15 StartY=2 StartZ=0 EndX=-64.15 EndY=30.5 EndZ=0
    g7: LineSegment StartX=-64.15 StartY=30.5 StartZ=0 EndX=-51.15 EndY=30.5 EndZ=0
    g8: LineSegment StartX=-51.15 StartY=30.5 StartZ=0 EndX=-51.15 EndY=2 EndZ=0
    g9: LineSegment StartX=-50.15 StartY=21.2866 StartZ=0 EndX=-50.15 EndY=-6.28659 EndZ=0
  constraints (26):
    c: Coincident(g1,g2)
    c: Coincident(g2,g0)
    c: Horizontal(g0)
    c: Horizontal(g1)
    c: Coincident(g0,g-5)
    c: Coincident(g4,g3)
    c: Coincident(g0,g3)
    c: Coincident(g1,g3)
    c: Coincident(g-5,g1)
    c: DistanceX(g3) = -35.1544
    c: DistanceY(g3) = 7.5
    c: Coincident(g5,g6)
    c: Coincident(g6,g7)
    c: Coincident(g7,g8)
    c: Coincident(g8,g5)
    c: Horizontal(g5)
    c: Vertical(g6)
    c: Coincident(g5,g-4)
    c: Coincident(g7,g-4)
    c: PointOnObject(g4,g-3)
    c: Coincident(g9,g4)
    c: Coincident(g9,g4)
    c: Vertical(g9)
    c: Diameter(g4) = 40.74
    c: Diameter(g3) = 56.51
    c: Coincident(g6,g-6)
FEATURE [PartDesign::Pad] Pad038
  BaseFeature = -> Pad037
  Length = 11
  Length2 = 100
  Profile = -> Sketch071
  Reversed = true
  Type = 0
FEATURE [Sketcher::SketchObject] Sketch072
  AttachmentOffset = pos=(0,0,-1) rot=(0,0,1;0rad)
  ExternalGeometry = -> [Sketch071]
  MapMode = 5
  Placement = pos=(0,0,-13) rot=(1,0,0;3.14159rad)
  Support = -> [DatumPlane030]
  sketch-geometry (5):
    g0: Circle CenterX=-35.1544 CenterY=7.5 CenterZ=0 NormalX=0 NormalY=0 NormalZ=1 AngleXU=0 Radius=27.255
    g1: ArcOfCircle CenterX=-35.1544 CenterY=7.5 CenterZ=0 NormalX=0 NormalY=0 NormalZ=1 AngleXU=0 Radius=21.37 StartAngle=3.86658 EndAngle=8.69979
    g2: LineSegment StartX=-51.15 StartY=21.6711 StartZ=0 EndX=-51.15 EndY=-6.67106 EndZ=0
    g3: LineSegment [constr] StartX=-14.7844 StartY=7.5 StartZ=0 EndX=-13.7844 EndY=7.5 EndZ=0
    g4: LineSegment [constr] StartX=-7.89944 StartY=7.5 StartZ=0 EndX=-6.89944 EndY=7.5 EndZ=0
  constraints (17):
    c: Coincident(g0,g-3)
    c: Coincident(g1,g0)
    c: PointOnObject(g2,g-4)
    c: Vertical(g2)
    c: Coincident(g1,g2)
    c: Coincident(g1,g2)
    c: Coincident(g1,g2)
    c: PointOnObject(g3,g-5)
    c: PointOnObject(g3,g1)
    c: Horizontal(g3)
    c: PointOnObject(g4,g0)
    c: PointOnObject(g4,g-3)
    c: Horizontal(g4)
    c: PointOnObject(g0,g3)
    c: PointOnObject(g0,g4)
    c: DistanceX(g3,g3) = 1
    c: DistanceX(g4,g4) = 1
FEATURE [PartDesign::Pocket] Pocket007018
  BaseFeature = -> Pad038
  Length = 9
  Length2 = 100
  Profile = -> Sketch072
  Type = 0
  expr: Length = Pad038.Length - 2mm
FEATURE [PartDesign::Line] DatumLine007
  AttacherType = Attacher::AttachEngineLine
  MapMode = 19
  Placement = pos=(-35.1544,-7.5,-14) rot=(0.363209,0.931708,0;3.14159rad)
  Support = -> [Sketch071]
FEATURE [Sketcher::SketchObject] Sketch073
  AttachmentOffset = pos=(-3,-10,-35) rot=(0,0,1;0rad)
  ExternalGeometry = -> [DatumLine007,Sketch072]
  MapMode = 5
  Placement = pos=(-35,-3,-10) rot=(0.57735,0.57735,0.57735;2.0944rad)
  Support = -> [YZ_Plane007]
  expr: Constraints[7] = Pad038.Length
  sketch-geometry (5):
    g0: LineSegment StartX=8.89154 StartY=2.59084 StartZ=0 EndX=15.8915 EndY=7.09084 EndZ=0
    g1: LineSegment StartX=15.8915 StartY=7.09084 StartZ=0 EndX=15.8915 EndY=-3.90916 EndZ=0
    g2: LineSegment StartX=15.8915 StartY=-3.90916 StartZ=0 EndX=8.89154 EndY=-3.90916 EndZ=0
    g3: LineSegment StartX=8.89154 StartY=-3.90916 StartZ=0 EndX=8.89154 EndY=2.59084 EndZ=0
    g4: LineSegment [constr] StartX=-8.27655 StartY=-5.53197 StartZ=0 EndX=15.8915 EndY=7.09084 EndZ=0
  constraints (11):
    c: Coincident(g0,g1)
    c: Coincident(g1,g2)
    c: Coincident(g2,g3)
    c: Coincident(g3,g0)
    c: Horizontal(g2)
    c: Vertical(g1)
    c: Vertical(g3)
    c: Distance(g1) = 11
    c: DistanceY(g3,g3) = 6.5
    c: DistanceX(g2,g2) = 7
    c: Coincident(g4,g0)
FEATURE [Sketcher::SketchObject] Sketch075
  ExternalGeometry = -> [Sketch071]
  MapMode = 5
  Placement = pos=(0,0,-14) rot=(1,0,0;3.14159rad)
  sketch-geometry (4):
    g0: LineSegment StartX=-65.15 StartY=31.5 StartZ=0 EndX=-50.15 EndY=31.5 EndZ=0
    g1: LineSegment StartX=-50.15 StartY=31.5 StartZ=0 EndX=-50.15 EndY=1 EndZ=0
    g2: LineSegment StartX=-50.15 StartY=1 StartZ=0 EndX=-65.15 EndY=1 EndZ=0
    g3: LineSegment StartX=-65.15 StartY=1 StartZ=0 EndX=-65.15 EndY=31.5 EndZ=0
  constraints (10):
    c: Coincident(g0,g1)
    c: Coincident(g1,g2)
    c: Coincident(g2,g3)
    c: Coincident(g3,g0)
    c: Horizontal(g0)
    c: Horizontal(g2)
    c: Vertical(g1)
    c: Coincident(g0,g-3)
    c: PointOnObject(g1,g-4)
    c: Coincident(g2,g-5)
FEATURE [PartDesign::Pad] Pad039
  BaseFeature = -> Pocket007018
  Length = 0.75
  Length2 = 100
  Profile = -> Sketch075
  Reversed = true
  Type = 0
FEATURE [PartDesign::Revolution] Revolution
  Angle = 55
  Axis = (-2e-16,-3e-16,-1)
  Base = (-35.1544,-7.5,-14)
  BaseFeature = -> Pad039
  Midplane = true
  Profile = -> Sketch073
  ReferenceAxis = -> DatumLine007
  Reversed = true
FEATURE [PartDesign::PolarPattern] PolarPattern
  Angle = 360
  Axis = -> DatumLine007
  BaseFeature = -> Revolution
  Occurrences = 2
  Originals = -> [Revolution]
FEATURE [PartDesign::Plane] DatumPlane031
  Length = 24.6136
  MapMode = 13
  Placement = pos=(-35,10.5582,-8.07582) rot=(-0.57735,0.57735,0.57735;4.18879rad)
  ResizeMode = 0
  Support = -> [Sketch073]
  Width = 24.0554
FEATURE [Sketcher::SketchObject] Sketch076
  ExternalGeometry = -> [Sketch073,DatumLine007]
  MapMode = 5
  Placement = pos=(-35,10.5582,-8.07582) rot=(-0.57735,0.57735,0.57735;4.18879rad)
  Support = -> [DatumPlane031]
  sketch-geometry (10):
    g0: LineSegment [constr] StartX=18.0582 StartY=-11.8291 StartZ=0 EndX=-2.33333 EndY=5.16667 EndZ=0
    g1: LineSegment [constr] StartX=-1.69405 StartY=-3.74055 StartZ=0 EndX=18.3555 EndY=-17.589 EndZ=0
    g2: LineSegment StartX=-2.47989 StartY=4.41667 StartZ=0 EndX=-3.33333 EndY=4.41667 EndZ=0
    g3: LineSegment StartX=-3.33333 StartY=4.41667 StartZ=0 EndX=-3.33333 EndY=-5.08333 EndZ=0
    g4: LineSegment StartX=-3.33333 StartY=-5.08333 StartZ=0 EndX=0.25 EndY=-5.08333 EndZ=0
    g5: LineSegment StartX=0.25 StartY=-5.08333 StartZ=0 EndX=5.43925 EndY=-8.6676 EndZ=0
    g6: LineSegment StartX=5.43925 StartY=-8.6676 StartZ=0 EndX=5.43925 EndY=-3.39811 EndZ=0
    g7: LineSegment StartX=-2.47989 StartY=4.41667 StartZ=0 EndX=2.34423 EndY=1.26806 EndZ=0
    g8: LineSegment StartX=2.34423 StartY=1.26806 StartZ=0 EndX=5.43925 EndY=-3.39811 EndZ=0
    g9: GeomPoint X=18.0582 Y=-7.77396 Z=0
  constraints (22):
    c: PointOnObject(g0,g-7)
    c: Coincident(g0,g-5)
    c: Horizontal(g2)
    c: Coincident(g2,g3)
    c: Vertical(g3)
    c: Coincident(g3,g4)
    c: Horizontal(g4)
    c: Coincident(g4,g5)
    c: PointOnObject(g5,g1)
    c: Coincident(g5,g6)
    c: Vertical(g6)
    c: DistanceY(g-6,g4) = 0.75
    c: PointOnObject(g4,g1)
    c: DistanceX(g3,g-6) = 1
    c: Coincident(g7,g8)
    c: Coincident(g8,g6)
    c: PointOnObject(g7,g0)
    c: DistanceY(g2,g0) = 0.75
    c: Coincident(g2,g7)
    c: Distance(g7,g-5) = 0.75
    c: PointOnObject(g9,g-7)
    c: DistanceX(g-1,g4) = 0.25
FEATURE [PartDesign::Groove] Groove
  Angle = 46
  Axis = (-2e-16,-3e-16,-1)
  Base = (-35.1544,-7.5,-14)
  BaseFeature = -> PolarPattern
  Midplane = true
  Profile = -> Sketch076
  ReferenceAxis = -> DatumLine007
FEATURE [PartDesign::PolarPattern] PolarPattern001
  Angle = 360
  Axis = -> DatumLine007
  BaseFeature = -> Groove
  Occurrences = 2
  Originals = -> [Groove]
FEATURE [PartDesign::Pocket] Pocket007019
  BaseFeature = -> PolarPattern001
  Length = 5
  Length2 = 100
  Profile = -> Sketch077
  Type = 1
FEATURE [App::DocumentObjectGroup] Gruppe004  label="Left-Fan-Assembly"
  Group = -> [Body001,Body002]
FEATURE [PartDesign::Plane] DatumPlane034
  Length = 24
  MapMode = 2
  ResizeMode = 0
  Support = -> [Sketch061]
  Width = 24
FEATURE [Sketcher::SketchObject] Sketch081
  ExternalGeometry = -> [Sketch061]
  MapMode = 5
  Support = -> [DatumPlane034]
  sketch-geometry (6):
    g0: Circle CenterX=-57.65 CenterY=-3.6 CenterZ=0 NormalX=0 NormalY=0 NormalZ=1 AngleXU=0 Radius=0.75
    g1: Circle CenterX=-57.65 CenterY=-29.4 CenterZ=0 NormalX=0 NormalY=0 NormalZ=1 AngleXU=0 Radius=0.75
    g2: Circle CenterX=-51.75 CenterY=-21.9 CenterZ=0 NormalX=0 NormalY=0 NormalZ=1 AngleXU=0 Radius=0.75
    g3: Circle CenterX=-51.75 CenterY=-11.1 CenterZ=0 NormalX=0 NormalY=0 NormalZ=1 AngleXU=0 Radius=0.75
    g4: Circle CenterX=-63.55 CenterY=-11.1 CenterZ=0 NormalX=0 NormalY=0 NormalZ=1 AngleXU=0 Radius=0.75
    g5: Circle CenterX=-63.55 CenterY=-21.9 CenterZ=0 NormalX=0 NormalY=0 NormalZ=1 AngleXU=0 Radius=0.75
  constraints (17):
    c: PointOnObject(g1,g-4)
    c: PointOnObject(g2,g-6)
    c: PointOnObject(g3,g-6)
    c: PointOnObject(g4,g-5)
    c: PointOnObject(g5,g-5)
    c: Radius(g4) = 0.75
    c: Equal(g4,g0)
    c: Equal(g4,g3)
    c: Equal(g4,g2)
    c: Equal(g4,g1)
    c: Equal(g4,g5)
    c: Symmetric(g-5,g-6,g0)
    c: Vertical(g1,g0)
    c: Horizontal(g4,g3)
    c: Horizontal(g2,g5)
    c: DistanceY(g-5,g5) = 7.5
    c: DistanceY(g4,g-5) = 7.5
FEATURE [PartDesign::Pad] Pad042
  BaseFeature = -> Pocket007016
  Length = 7.5
  Length2 = 100
  Profile = -> Sketch081
  Type = 0
FEATURE [PartDesign::Pad] Pad034
  BaseFeature = -> Pad042
  Length = 1
  Length2 = 100
  Profile = -> Sketch065
  Reversed = true
  Type = 0
FEATURE [Sketcher::SketchObject] Sketch066
  ExternalGeometry = -> [Pad034]
  MapMode = 5
  Placement = pos=(0,0,7.5) rot=(0,0,1;0rad)
  Support = -> [Pad034]
  sketch-geometry (4):
    g0: LineSegment StartX=-64.55 StartY=1.4 StartZ=0 EndX=-50.75 EndY=1.4 EndZ=0
    g1: LineSegment StartX=-50.75 StartY=1.4 StartZ=0 EndX=-50.75 EndY=-3.6 EndZ=0
    g2: LineSegment StartX=-50.75 StartY=-3.6 StartZ=0 EndX=-64.55 EndY=-3.6 EndZ=0
    g3: LineSegment StartX=-64.55 StartY=-3.6 StartZ=0 EndX=-64.55 EndY=1.4 EndZ=0
  constraints (12):
    c: Coincident(g0,g1)
    c: Coincident(g1,g2)
    c: Coincident(g2,g3)
    c: Coincident(g3,g0)
    c: Horizontal(g0)
    c: Horizontal(g2)
    c: Vertical(g1)
    c: Vertical(g3)
    c: DistanceY(g3,g3) = 5
    c: DistanceY(g-3,g2) = 1
    c: DistanceX(g2,g-3) = 2
    c: DistanceX(g-4,g1) = 2
FEATURE [PartDesign::Pocket] Pocket007017
  BaseFeature = -> Pad034
  Length = 3
  Length2 = 100
  Profile = -> Sketch066
  Type = 0
FEATURE [PartDesign::Body] Body004  label="Left-Fan-Nozzle-Small-design"
  Group = -> [ShapeBinder003,Sketch061,Pad031,Sketch062,Pad032,DatumPlane026,Sketch063,Pad033,DatumPlane027,DatumPlane028,Sketch064,Pocket007016,Pad042,Sketch065,Pad034,Sketch066,Pocket007017,DatumPlane034,Sketch081]
  Placement = pos=(0,-32,-16.75) rot=(0,0,1;0rad)
  Tip = -> Pocket007017
FEATURE [Sketcher::SketchObject] Sketch082
  ExternalGeometry = -> [Pocket007019]
  MapMode = 5
  Placement = pos=(-25.23,-42.315,0) rot=(0.57735,0.57735,0.57735;2.0944rad)
  Support = -> [DatumPlane032]
  sketch-geometry (8):
    g0: LineSegment StartX=17.0262 StartY=-3 StartZ=0 EndX=9.43114 EndY=-3 EndZ=0
    g1: LineSegment StartX=9.43114 StartY=-3 StartZ=0 EndX=9.43114 EndY=-14 EndZ=0
    g2: LineSegment StartX=9.43114 StartY=-14 StartZ=0 EndX=17.0262 EndY=-14 EndZ=0
    g3: LineSegment StartX=17.0262 StartY=-14 StartZ=0 EndX=17.0262 EndY=-3 EndZ=0
    g4: LineSegment StartX=60.1989 StartY=-14 StartZ=0 EndX=52.6038 EndY=-14 EndZ=0
    g5: LineSegment StartX=52.6038 StartY=-14 StartZ=0 EndX=52.6038 EndY=-3 EndZ=0
    g6: LineSegment StartX=52.6038 StartY=-3 StartZ=0 EndX=60.1989 EndY=-3 EndZ=0
    g7: LineSegment StartX=60.1989 StartY=-3 StartZ=0 EndX=60.1989 EndY=-14 EndZ=0
  constraints (20):
    c: Coincident(g0,g1)
    c: Coincident(g1,g2)
    c: Coincident(g2,g3)
    c: Coincident(g3,g0)
    c: Horizontal(g0)
    c: Horizontal(g2)
    c: Vertical(g1)
    c: Coincident(g0,g-4)
    c: PointOnObject(g0,g-3)
    c: Coincident(g2,g-4)
    c: Coincident(g4,g5)
    c: Coincident(g5,g6)
    c: Coincident(g6,g7)
    c: Coincident(g7,g4)
    c: Horizontal(g4)
    c: Horizontal(g6)
    c: Vertical(g7)
    c: Coincident(g5,g-6)
    c: Coincident(g4,g-7)
    c: PointOnObject(g-5,g7)
FEATURE [PartDesign::Pad] Pad043
  BaseFeature = -> Pocket007019
  Length = 0.75
  Length2 = 100
  Profile = -> Sketch082
  Reversed = true
  Type = 0
FEATURE [PartDesign::Body] Body005  label="Left-Fan-Nozzle-180°-design"
  Group = -> [ShapeBinder004,Sketch067,Pad035,DatumPlane033,ShapeBinder005,Sketch068,Pad036,ShapeBinder006,Pad041,DatumPlane029,Sketch069,Pad037,DatumPlane030,Sketch071,Pad038,Sketch072,Pocket007018,Pad039,Sketch080,DatumLine007,Sketch073,Revolution,Sketch075,PolarPattern,DatumPlane031,Sketch076,Groove,PolarPattern001,Sketch077,Pocket007019,Sketch078,DatumPlane032,Sketch082,Pad043]
  Origin = -> Origin007
  Placement = pos=(0,-32,-16.75) rot=(0,0,1;0rad)
  Tip = -> Pad043
FEATURE [App::DocumentObjectGroup] Gruppe  label="Design"
  Group = -> [Body,Gruppe004,Body003,Body004,Body005]
FEATURE [Mesh::Feature] V6_6_Duct  label="E3E-V6.6_Duct"
  Placement = pos=(-35,-39.25,-13.5) rot=(0.57735,0.57735,0.57735;2.0944rad)
FEATURE [App::DocumentObjectGroup] Gruppe002  label="3rd-Party"
  Group = -> [titan_aero_holder_v5,_0mm_Fan001,Part,Fusion001,V6_6_Duct]
FEATURE [PartDesign::FeatureBase] Clone
  BaseFeature = -> Pocket007014
  Placement = pos=(0,0,0) rot=(1,0,0;1.5708rad)
FEATURE [PartDesign::Body] Body006  label="XY-Carrier"
  Group = -> [Clone]
  Origin = -> Origin008
  Placement = pos=(13,9,16) rot=(1,0,0;4.71239rad)
  Tip = -> Clone
FEATURE [PartDesign::FeatureBase] Clone001
  BaseFeature = -> Body001
  Placement = pos=(0,0,20) rot=(0,0,1;0rad)
FEATURE [PartDesign::Body] Body007  label="Left-Fan-Clamp1"
  Group = -> [Clone001]
  Origin = -> Origin009
  Tip = -> Clone001
FEATURE [PartDesign::FeatureBase] Clone002
  BaseFeature = -> Body002
  Placement = pos=(0,0,22) rot=(0,0,1;0rad)
FEATURE [PartDesign::Body] Body008  label="Left-Fan-Clamp2"
  Group = -> [Clone002]
  Origin = -> Origin010
  Placement = pos=(24,10,52) rot=(1,0,0;1.5708rad)
  Tip = -> Clone002
FEATURE [PartDesign::FeatureBase] Clone003
  BaseFeature = -> Body003
  Placement = pos=(0,-32,22) rot=(0,0,1;0rad)
FEATURE [PartDesign::Body] Body009  label="Left-Fan-Fanduct"
  Group = -> [Clone003]
  Origin = -> Origin011
  Placement = pos=(-22,-17,82) rot=(0,-1,0;1.5708rad)
  Tip = -> Clone003
FEATURE [PartDesign::FeatureBase] Clone004
  BaseFeature = -> Pocket007017
FEATURE [PartDesign::Body] Body010  label="Left-Fan-Nozzle-Small"
  Group = -> [Clone004]
  Origin = -> Origin012
  Placement = pos=(49,-8,30) rot=(0,0,1;0rad)
  Tip = -> Clone004
FEATURE [PartDesign::FeatureBase] Clone005
  BaseFeature = -> Body005
  Placement = pos=(0,-32,-16.75) rot=(0,0,1;0rad)
FEATURE [PartDesign::Body] Body011  label="Left-Fan-Nozzle-180°"
  Group = -> [Clone005]
  Origin = -> Origin013
  Placement = pos=(63,-15,41) rot=(0,0,1;0rad)
  Tip = -> Clone005
FEATURE [App::DocumentObjectGroup] Gruppe005  label="printables"
  Group = -> [Body006,Body007,Body008,Body009,Body010,Body011]
